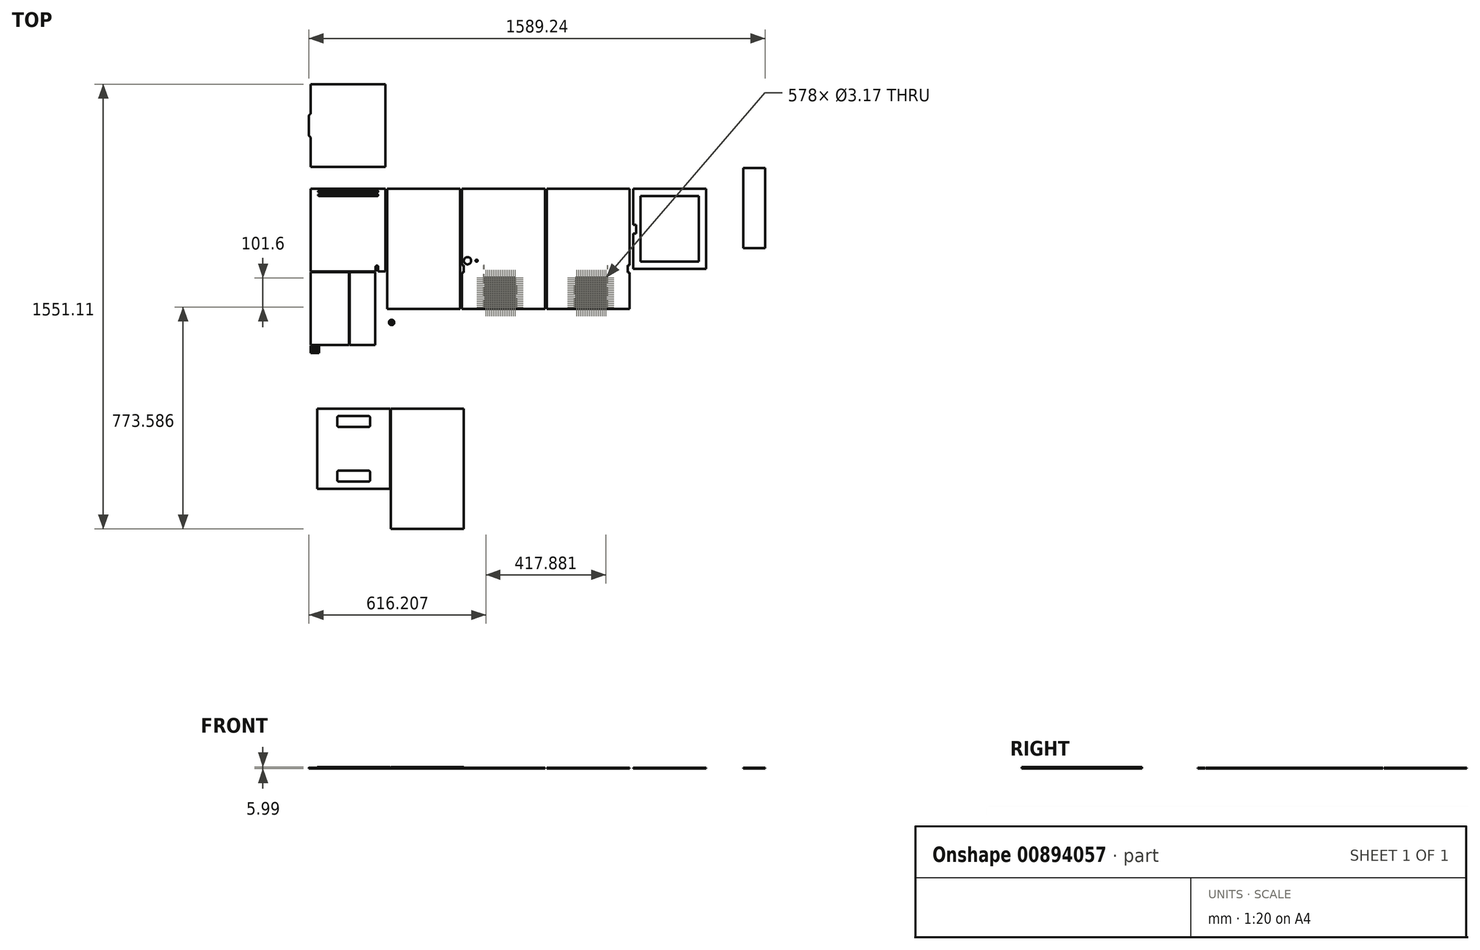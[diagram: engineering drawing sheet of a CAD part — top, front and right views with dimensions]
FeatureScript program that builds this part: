
annotation { "Feature Type Name" : "Feature", "Feature Type Description" : "" }
export const myFeature = defineFeature(function(context is Context, id is Id, definition is map)
    precondition{}
    {
        {
            var Q0;
            Q0=qCreatedBy(makeId("Top.planeOp"),FACE);
            var sketch = newSketch(context, id + "F0", { "sketchPlane" : qUnion([Q0])});
            skLineSegment(sketch, "E0.bottom", {"start": v(-364.9, 306.86) * mm, "end": v(-60.1, 306.86) * mm});
            skLineSegment(sketch, "E0.top", {"start": v(-364.9, -302.74) * mm, "end": v(-60.1, -302.74) * mm});
            skLineSegment(sketch, "E0.left", {"start": v(-364.9, 306.86) * mm, "end": v(-364.9, -302.74) * mm});
            skLineSegment(sketch, "E0.right", {"start": v(-60.1, 306.86) * mm, "end": v(-60.1, -302.74) * mm});
            skSolve(sketch);
        }
        {
            var Q0;
            Q0=makeQuery(id+"F0.imprint","IMPRINT",FACE,{"disambiguationData":[TD([[makeQuery(id+"F0.imprint","IMPRINT",EDGE,{"derivedFrom":sQuery(id+"F0.wireOp",EDGE,"E0.bottom")}),-1.0]])]});
            var sketch = newSketch(context, id + "F1", { "sketchPlane" : qUnion([Q0])});
            skPoint(sketch, "E1", {"position": v(-364.9, 306.86) * mm});
            skLineSegment(sketch, "E2.bottom", {"start": v(-364.9, 306.86) * mm, "end": v(-104.55, 306.86) * mm});
            skLineSegment(sketch, "E2.top", {"start": v(-364.9, 18.29) * mm, "end": v(-104.55, 18.29) * mm});
            skLineSegment(sketch, "E2.left", {"start": v(-364.9, 306.86) * mm, "end": v(-364.9, 18.29) * mm});
            skLineSegment(sketch, "E2.right", {"start": v(-104.55, 306.86) * mm, "end": v(-104.55, 18.29) * mm});
            skPoint(sketch, "E3", {"position": v(457.07, 306.86) * mm});
            skLineSegment(sketch, "E4.bottom", {"start": v(457.07, 306.86) * mm, "end": v(745.64, 306.86) * mm});
            skLineSegment(sketch, "E4.top", {"start": v(457.07, -112.24) * mm, "end": v(745.64, -112.24) * mm});
            skLineSegment(sketch, "E4.left", {"start": v(457.07, 306.86) * mm, "end": v(457.07, -112.24) * mm});
            skLineSegment(sketch, "E4.right", {"start": v(745.64, 306.86) * mm, "end": v(745.64, 40.16) * mm});
            skLineSegment(sketch, "E5.bottom", {"start": v(162.15, 306.86) * mm, "end": v(450.72, 306.86) * mm});
            skLineSegment(sketch, "E5.top", {"start": v(162.15, -112.24) * mm, "end": v(450.72, -112.24) * mm});
            skLineSegment(sketch, "E5.left", {"start": v(162.15, 306.86) * mm, "end": v(162.15, 40.16) * mm});
            skLineSegment(sketch, "E5.right", {"start": v(450.72, 306.86) * mm, "end": v(450.72, -112.24) * mm});
            skLineSegment(sketch, "E6.bottom", {"start": v(-98.2, 306.86) * mm, "end": v(155.8, 306.86) * mm});
            skLineSegment(sketch, "E6.top", {"start": v(-98.2, -112.24) * mm, "end": v(155.8, -112.24) * mm});
            skLineSegment(sketch, "E6.left", {"start": v(-98.2, 306.86) * mm, "end": v(-98.2, -112.24) * mm});
            skLineSegment(sketch, "E6.right", {"start": v(155.8, 306.86) * mm, "end": v(155.8, -112.24) * mm});
            skPoint(sketch, "E7", {"position": v(-229, 15.75) * mm});
            skLineSegment(sketch, "E8.bottom", {"start": v(-229, 15.75) * mm, "end": v(-140.1, 15.75) * mm});
            skLineSegment(sketch, "E8.top", {"start": v(-229, -238.25) * mm, "end": v(-140.1, -238.25) * mm});
            skLineSegment(sketch, "E8.left", {"start": v(-229, 15.75) * mm, "end": v(-229, -238.25) * mm});
            skLineSegment(sketch, "E8.right", {"start": v(-140.1, 15.75) * mm, "end": v(-140.1, -238.25) * mm});
            skLineSegment(sketch, "E9.bottom", {"start": v(162.15, 40.16) * mm, "end": v(168.5, 40.16) * mm});
            skLineSegment(sketch, "E9.top", {"start": v(162.15, 14.76) * mm, "end": v(168.5, 14.76) * mm});
            skLineSegment(sketch, "E9.right", {"start": v(168.5, 40.16) * mm, "end": v(168.5, 14.76) * mm});
            skLineSegment(sketch, "E10.trimOffspring", {"start": v(162.15, 14.76) * mm, "end": v(162.15, -112.24) * mm});
            skLineSegment(sketch, "E11", {"start": v(745.64, 40.16) * mm, "end": v(739.3, 40.16) * mm});
            skLineSegment(sketch, "E12", {"start": v(739.3, 40.16) * mm, "end": v(739.3, 14.76) * mm});
            skLineSegment(sketch, "E13", {"start": v(739.3, 14.76) * mm, "end": v(745.64, 14.76) * mm});
            skLineSegment(sketch, "E14.trimOffspring", {"start": v(745.64, 14.76) * mm, "end": v(745.64, -112.24) * mm});
            skLineSegment(sketch, "E15.bottom", {"start": v(-364.9, -238.25) * mm, "end": v(-231.55, -238.25) * mm});
            skLineSegment(sketch, "E15.top", {"start": v(-364.9, 15.75) * mm, "end": v(-231.55, 15.75) * mm});
            skLineSegment(sketch, "E15.left", {"start": v(-364.9, -238.25) * mm, "end": v(-364.9, 15.75) * mm});
            skLineSegment(sketch, "E15.right", {"start": v(-231.55, -238.25) * mm, "end": v(-231.55, 15.75) * mm});
            skCircle(sketch, "E16", {"center": v(-83.43, -156.52) * mm, "radius": 3.75 * mm});
            skCircle(sketch, "E17", {"center": v(-83.43, -164.32) * mm, "radius": 1.5 * mm});
            skCircle(sketch, "E18", {"center": v(-83.43, -159.38) * mm, "radius": 9.35 * mm});
            skLineSegment(sketch, "E19.bottom", {"start": v(-364.9, -240.8) * mm, "end": v(-358.55, -240.8) * mm});
            skLineSegment(sketch, "E19.top", {"start": v(-364.9, -266.2) * mm, "end": v(-358.55, -266.2) * mm});
            skLineSegment(sketch, "E19.left", {"start": v(-364.9, -240.8) * mm, "end": v(-364.9, -266.2) * mm});
            skLineSegment(sketch, "E19.right", {"start": v(-358.55, -240.8) * mm, "end": v(-358.55, -266.2) * mm});
            skLineSegment(sketch, "E20.bottom", {"start": v(-336.32, 300.5) * mm, "end": v(-133.12, 300.5) * mm});
            skLineSegment(sketch, "E20.top", {"start": v(-336.32, 294.16) * mm, "end": v(-133.12, 294.16) * mm});
            skLineSegment(sketch, "E21", {"start": v(-234.72, 306.86) * mm, "end": v(-234.72, 18.29) * mm, "construction": true});
            skPoint(sketch, "E22", {"position": v(-234.72, 300.5) * mm});
            skArc(sketch, "E23", {"start": v(-133.12, 294.16) * mm, "mid": v(-129.95, 297.33) * mm, "end": v(-133.12, 300.5) * mm});
            skArc(sketch, "E24", {"start": v(-336.32, 300.5) * mm, "mid": v(-339.5, 297.33) * mm, "end": v(-336.32, 294.16) * mm});
            skArc(sketch, "E25.0.1.0", {"start": v(-336.32, 287.8) * mm, "mid": v(-339.5, 284.63) * mm, "end": v(-336.32, 281.46) * mm});
            skLineSegment(sketch, "E25.0.1.1", {"start": v(-336.32, 287.8) * mm, "end": v(-133.12, 287.8) * mm});
            skArc(sketch, "E25.0.1.2", {"start": v(-133.12, 281.46) * mm, "mid": v(-129.95, 284.63) * mm, "end": v(-133.12, 287.8) * mm});
            skLineSegment(sketch, "E25.0.1.3", {"start": v(-336.32, 281.46) * mm, "end": v(-133.12, 281.46) * mm});
            skLineSegment(sketch, "E25.direction1", {"start": v(-336.32, 294.16) * mm, "end": v(-295.94, 294.16) * mm, "construction": true});
            skLineSegment(sketch, "E25.direction2", {"start": v(-336.32, 294.16) * mm, "end": v(-336.32, 281.46) * mm, "construction": true});
            skLineSegment(sketch, "E26.bottom", {"start": v(-129.95, 18.29) * mm, "end": v(-139.47, 18.29) * mm});
            skLineSegment(sketch, "E26.left", {"start": v(-129.95, 18.29) * mm, "end": v(-129.95, 34.16) * mm});
            skLineSegment(sketch, "E26.right", {"start": v(-139.47, 18.29) * mm, "end": v(-139.47, 34.16) * mm});
            skArc(sketch, "E27", {"start": v(-129.95, 34.16) * mm, "mid": v(-134.7, 38.92) * mm, "end": v(-139.47, 34.16) * mm});
            skLineSegment(sketch, "E28.1.0.0", {"start": v(-357.28, -240.8) * mm, "end": v(-357.28, -266.2) * mm});
            skLineSegment(sketch, "E28.1.0.1", {"start": v(-357.28, -240.8) * mm, "end": v(-350.93, -240.8) * mm});
            skLineSegment(sketch, "E28.1.0.2", {"start": v(-350.93, -240.8) * mm, "end": v(-350.93, -266.2) * mm});
            skLineSegment(sketch, "E28.1.0.3", {"start": v(-357.28, -266.2) * mm, "end": v(-350.93, -266.2) * mm});
            skLineSegment(sketch, "E28.2.0.0", {"start": v(-349.66, -240.8) * mm, "end": v(-349.66, -266.2) * mm});
            skLineSegment(sketch, "E28.2.0.1", {"start": v(-349.66, -240.8) * mm, "end": v(-343.3, -240.8) * mm});
            skLineSegment(sketch, "E28.2.0.2", {"start": v(-343.3, -240.8) * mm, "end": v(-343.3, -266.2) * mm});
            skLineSegment(sketch, "E28.2.0.3", {"start": v(-349.66, -266.2) * mm, "end": v(-343.3, -266.2) * mm});
            skLineSegment(sketch, "E28.3.0.0", {"start": v(-342.04, -240.8) * mm, "end": v(-342.04, -266.2) * mm});
            skLineSegment(sketch, "E28.3.0.1", {"start": v(-342.04, -240.8) * mm, "end": v(-335.69, -240.8) * mm});
            skLineSegment(sketch, "E28.3.0.2", {"start": v(-335.69, -240.8) * mm, "end": v(-335.69, -266.2) * mm});
            skLineSegment(sketch, "E28.3.0.3", {"start": v(-342.04, -266.2) * mm, "end": v(-335.69, -266.2) * mm});
            skLineSegment(sketch, "E28.direction1", {"start": v(-364.9, -266.2) * mm, "end": v(-357.28, -266.2) * mm, "construction": true});
            skLineSegment(sketch, "E29.bottom", {"start": v(758.34, 306.86) * mm, "end": v(1012.34, 306.86) * mm});
            skLineSegment(sketch, "E29.top", {"start": v(758.34, 27.46) * mm, "end": v(1012.34, 27.46) * mm});
            skLineSegment(sketch, "E29.left", {"start": v(758.34, 306.86) * mm, "end": v(758.34, 27.46) * mm});
            skLineSegment(sketch, "E29.right", {"start": v(1012.34, 306.86) * mm, "end": v(1012.34, 27.46) * mm});
            skLineSegment(sketch, "E30.0", {"start": v(783.74, 281.46) * mm, "end": v(986.94, 281.46) * mm});
            skLineSegment(sketch, "E30.1", {"start": v(783.74, 281.46) * mm, "end": v(783.74, 52.86) * mm});
            skLineSegment(sketch, "E30.2", {"start": v(783.74, 52.86) * mm, "end": v(986.94, 52.86) * mm});
            skLineSegment(sketch, "E30.3", {"start": v(986.94, 281.46) * mm, "end": v(986.94, 52.86) * mm});
            skLineSegment(sketch, "E31.bottom", {"start": v(758.34, 181.62) * mm, "end": v(768.58, 181.62) * mm});
            skLineSegment(sketch, "E31.top", {"start": v(758.34, 151.14) * mm, "end": v(768.58, 151.14) * mm});
            skLineSegment(sketch, "E31.left", {"start": v(758.34, 181.62) * mm, "end": v(758.34, 151.14) * mm});
            skLineSegment(sketch, "E31.right", {"start": v(768.58, 181.62) * mm, "end": v(768.58, 151.14) * mm});
            skLineSegment(sketch, "E32.bottom", {"start": v(1141.79, 379.02) * mm, "end": v(1217.99, 379.02) * mm});
            skLineSegment(sketch, "E32.top", {"start": v(1141.79, 99.62) * mm, "end": v(1217.99, 99.62) * mm});
            skLineSegment(sketch, "E32.left", {"start": v(1141.79, 379.02) * mm, "end": v(1141.79, 99.62) * mm});
            skLineSegment(sketch, "E32.right", {"start": v(1217.99, 379.02) * mm, "end": v(1217.99, 99.62) * mm});
            skSolve(sketch);
        }
        {
            var Q0;
            Q0=makeQuery(id+"F1.imprint","IMPRINT",FACE,{"disambiguationData":[TD([[makeQuery(id+"F1.imprint","IMPRINT",EDGE,{"derivedFrom":sQuery(id+"F1.wireOp",EDGE,"E2.bottom")}),-1.0]])]});
            var Q1;
            Q1=makeQuery(id+"F1.imprint","IMPRINT",FACE,{"disambiguationData":[TD([[makeQuery(id+"F1.imprint","IMPRINT",EDGE,{"derivedFrom":sQuery(id+"F1.wireOp",EDGE,"E6.bottom")}),-1.0]])]});
            var Q2;
            Q2=makeQuery(id+"F1.imprint","IMPRINT",FACE,{"disambiguationData":[TD([[makeQuery(id+"F1.imprint","IMPRINT",EDGE,{"derivedFrom":sQuery(id+"F1.wireOp",EDGE,"E4.bottom")}),-1.0]])]});
            var Q3;
            Q3=makeQuery(id+"F1.imprint","IMPRINT",FACE,{"disambiguationData":[TD([[makeQuery(id+"F1.imprint","IMPRINT",EDGE,{"derivedFrom":sQuery(id+"F1.wireOp",EDGE,"E5.bottom")}),-1.0]])]});
            var Q4;
            Q4=makeQuery(id+"F1.imprint","IMPRINT",FACE,{"disambiguationData":[TD([[makeQuery(id+"F1.imprint","IMPRINT",EDGE,{"derivedFrom":sQuery(id+"F1.wireOp",EDGE,"E8.bottom")}),-1.0]])]});
            var Q5;
            Q5=makeQuery(id+"F1.imprint","IMPRINT",FACE,{"disambiguationData":[TD([[makeQuery(id+"F1.imprint","IMPRINT",EDGE,{"derivedFrom":sQuery(id+"F1.wireOp",EDGE,"E15.bottom")}),1.0]])]});
            var Q6;
            Q6=makeQuery(id+"F1.imprint","IMPRINT",FACE,{"disambiguationData":[TD([[makeQuery(id+"F1.imprint","IMPRINT",EDGE,{"derivedFrom":sQuery(id+"F1.wireOp",EDGE,"E16")}),-1.0]])]});
            var Q7;
            Q7=makeQuery(id+"F1.imprint","IMPRINT",FACE,{"disambiguationData":[TD([[makeQuery(id+"F1.imprint","IMPRINT",EDGE,{"derivedFrom":sQuery(id+"F1.wireOp",EDGE,"E19.bottom")}),-1.0]])]});
            var Q8;
            Q8=makeQuery(id+"F1.imprint","IMPRINT",FACE,{"disambiguationData":[TD([[makeQuery(id+"F1.imprint","IMPRINT",EDGE,{"derivedFrom":sQuery(id+"F1.wireOp",EDGE,"IQMkBjuR-eJGy-Trob-1RJN-rlCJfxQlDLsO.bottom")}),-1.0]])]});
            var Q9;
            Q9=makeQuery(id+"F1.imprint","IMPRINT",FACE,{"disambiguationData":[TD([[makeQuery(id+"F1.imprint","IMPRINT",EDGE,{"derivedFrom":sQuery(id+"F1.wireOp",EDGE,"E28.1.0.0")}),1.0]])]});
            var Q10;
            Q10=makeQuery(id+"F1.imprint","IMPRINT",FACE,{"disambiguationData":[TD([[makeQuery(id+"F1.imprint","IMPRINT",EDGE,{"derivedFrom":sQuery(id+"F1.wireOp",EDGE,"E28.2.0.0")}),1.0]])]});
            var Q11;
            Q11=makeQuery(id+"F1.imprint","IMPRINT",FACE,{"disambiguationData":[TD([[makeQuery(id+"F1.imprint","IMPRINT",EDGE,{"derivedFrom":sQuery(id+"F1.wireOp",EDGE,"E28.3.0.0")}),1.0]])]});
            var Q12;
            Q12=makeQuery(id+"F1.imprint","IMPRINT",FACE,{"disambiguationData":[TD([[makeQuery(id+"F1.imprint","IMPRINT",EDGE,{"derivedFrom":sQuery(id+"F1.wireOp",EDGE,"E29.bottom")}),-1.0]])]});
            var Q13;
            Q13=makeQuery(id+"F1.imprint","IMPRINT",FACE,{"disambiguationData":[TD([[makeQuery(id+"F1.imprint","IMPRINT",EDGE,{"derivedFrom":sQuery(id+"F1.wireOp",EDGE,"E32.bottom")}),-1.0]])]});
            extrude(context, id + "F2", {"entities" : qUnion([Q0, Q1, Q2, Q3, Q4, Q5, Q6, Q7, Q8, Q9, Q10, Q11, Q12, Q13]), "depth" : 3.17 * mm, "offsetDistance" : 25.4 * mm});
        }
        {
            var Q0;
            Q0=qCreatedBy(makeId("Top.planeOp"),FACE);
            var sketch = newSketch(context, id + "F3", { "sketchPlane" : qUnion([Q0])});
            skLineSegment(sketch, "E33.bottom", {"start": v(-342.67, -460.38) * mm, "end": v(266.93, -460.38) * mm});
            skLineSegment(sketch, "E33.top", {"start": v(-342.67, -1069.98) * mm, "end": v(266.93, -1069.98) * mm});
            skLineSegment(sketch, "E33.left", {"start": v(-342.67, -460.38) * mm, "end": v(-342.67, -1069.98) * mm});
            skLineSegment(sketch, "E33.right", {"start": v(266.93, -460.38) * mm, "end": v(266.93, -1069.98) * mm});
            skSolve(sketch);
        }
        {
            var Q0;
            Q0=makeQuery(id+"F3.imprint","IMPRINT",FACE,{"disambiguationData":[TD([[makeQuery(id+"F3.imprint","IMPRINT",EDGE,{"derivedFrom":sQuery(id+"F3.wireOp",EDGE,"E33.bottom")}),-1.0]])]});
            var sketch = newSketch(context, id + "F4", { "sketchPlane" : qUnion([Q0])});
            skPoint(sketch, "E34", {"position": v(-342.67, -460.38) * mm});
            skLineSegment(sketch, "E35.bottom", {"start": v(-342.67, -460.38) * mm, "end": v(-88.67, -460.38) * mm});
            skLineSegment(sketch, "E35.top", {"start": v(-342.67, -739.78) * mm, "end": v(-88.67, -739.78) * mm});
            skLineSegment(sketch, "E35.left", {"start": v(-342.67, -460.38) * mm, "end": v(-342.67, -739.78) * mm});
            skLineSegment(sketch, "E35.right", {"start": v(-88.67, -460.38) * mm, "end": v(-88.67, -739.78) * mm});
            skLineSegment(sketch, "E36", {"start": v(-215.67, -460.38) * mm, "end": v(-215.67, -739.78) * mm, "construction": true});
            skLineSegment(sketch, "E37.bottom", {"start": v(-158.52, -485.78) * mm, "end": v(-272.82, -485.78) * mm});
            skLineSegment(sketch, "E37.top", {"start": v(-158.52, -523.88) * mm, "end": v(-272.82, -523.88) * mm});
            skLineSegment(sketch, "E37.left", {"start": v(-158.52, -485.78) * mm, "end": v(-158.52, -523.88) * mm});
            skLineSegment(sketch, "E37.right", {"start": v(-272.82, -485.78) * mm, "end": v(-272.82, -523.88) * mm});
            skPoint(sketch, "E37.middle", {"position": v(-215.67, -504.83) * mm});
            skLineSegment(sketch, "E38.bottom", {"start": v(-158.52, -676.28) * mm, "end": v(-272.82, -676.28) * mm});
            skLineSegment(sketch, "E38.top", {"start": v(-158.52, -714.38) * mm, "end": v(-272.82, -714.38) * mm});
            skLineSegment(sketch, "E38.left", {"start": v(-158.52, -676.28) * mm, "end": v(-158.52, -714.38) * mm});
            skLineSegment(sketch, "E38.right", {"start": v(-272.82, -676.28) * mm, "end": v(-272.82, -714.38) * mm});
            skPoint(sketch, "E38.middle", {"position": v(-215.67, -695.33) * mm});
            skPoint(sketch, "E39", {"position": v(-85.5, -460.38) * mm});
            skLineSegment(sketch, "E40.bottom", {"start": v(-85.5, -460.38) * mm, "end": v(168.5, -460.38) * mm});
            skLineSegment(sketch, "E40.top", {"start": v(-85.5, -879.48) * mm, "end": v(168.5, -879.48) * mm});
            skLineSegment(sketch, "E40.left", {"start": v(-85.5, -460.38) * mm, "end": v(-85.5, -879.48) * mm});
            skLineSegment(sketch, "E40.right", {"start": v(168.5, -460.38) * mm, "end": v(168.5, -879.48) * mm});
            skSolve(sketch);
        }
        {
            var Q0;
            Q0 = qSketchRegion(id + "F4", true);
            extrude(context, id + "F5", {"entities" : qUnion([Q0]), "depth" : 6 * mm, "offsetDistance" : 25.4 * mm});
        }
        {
            var Q0;
            Q0=makeQuery(id+"F2.opExtrude","CAP_FACE",FACE,{"disambiguationData":[OSD([sQuery(id+"F1.wireOp",EDGE,"E5.bottom"),sQuery(id+"F1.wireOp",EDGE,"E5.top"),sQuery(id+"F1.wireOp",EDGE,"E5.left"),sQuery(id+"F1.wireOp",EDGE,"E5.right"),sQuery(id+"F1.wireOp",EDGE,"E9.bottom"),sQuery(id+"F1.wireOp",EDGE,"E9.top"),sQuery(id+"F1.wireOp",EDGE,"E9.right"),sQuery(id+"F1.wireOp",EDGE,"E10.trimOffspring")])],"isStart":true});
            var sketch = newSketch(context, id + "F6", { "sketchPlane" : qUnion([Q0])});
            skLineSegment(sketch, "E41.bottom", {"start": v(353.03, 104.4) * mm, "end": v(353.29, 104.4) * mm});
            skLineSegment(sketch, "E41.top", {"start": v(353.03, 15.5) * mm, "end": v(353.29, 15.5) * mm});
            skLineSegment(sketch, "E41.left", {"start": v(353.03, 104.4) * mm, "end": v(353.03, 15.5) * mm});
            skLineSegment(sketch, "E41.right", {"start": v(353.29, 104.4) * mm, "end": v(353.29, 15.5) * mm});
            skLineSegment(sketch, "E42.bottom", {"start": v(238.6, 112.24) * mm, "end": v(238.35, 112.24) * mm});
            skLineSegment(sketch, "E42.top", {"start": v(238.6, -40.16) * mm, "end": v(238.35, -40.16) * mm});
            skLineSegment(sketch, "E42.left", {"start": v(238.6, 112.24) * mm, "end": v(238.6, -40.16) * mm});
            skLineSegment(sketch, "E42.right", {"start": v(238.35, 112.24) * mm, "end": v(238.35, -40.16) * mm});
            skSolve(sketch);
        }
        {
            var Q0;
            Q0 = qSketchRegion(id + "F6", true);
            extrude(context, id + "F7", {"entities" : qUnion([Q0]), "operationType" : NewBodyOperationType.REMOVE, "oppositeDirection" : true, "depth" : 0.5 * mm, "offsetDistance" : 25.4 * mm});
        }
        {
            var Q0;
            Q0=makeQuery(id+"F2.opExtrude","CAP_FACE",FACE,{"disambiguationData":[OSD([sQuery(id+"F1.wireOp",EDGE,"E4.bottom"),sQuery(id+"F1.wireOp",EDGE,"E4.top"),sQuery(id+"F1.wireOp",EDGE,"E4.left"),sQuery(id+"F1.wireOp",EDGE,"E4.right"),sQuery(id+"F1.wireOp",EDGE,"E11"),sQuery(id+"F1.wireOp",EDGE,"E12"),sQuery(id+"F1.wireOp",EDGE,"E13"),sQuery(id+"F1.wireOp",EDGE,"E14.trimOffspring")])],"isStart":true});
            var sketch = newSketch(context, id + "F8", { "sketchPlane" : qUnion([Q0])});
            skLineSegment(sketch, "E43.bottom", {"start": v(554.5, 104.4) * mm, "end": v(554.76, 104.4) * mm});
            skLineSegment(sketch, "E43.top", {"start": v(554.5, 15.5) * mm, "end": v(554.76, 15.5) * mm});
            skLineSegment(sketch, "E43.left", {"start": v(554.5, 104.4) * mm, "end": v(554.5, 15.5) * mm});
            skLineSegment(sketch, "E43.right", {"start": v(554.76, 104.4) * mm, "end": v(554.76, 15.5) * mm});
            skLineSegment(sketch, "E44.bottom", {"start": v(669.19, 112.24) * mm, "end": v(669.44, 112.24) * mm});
            skLineSegment(sketch, "E44.top", {"start": v(669.19, -40.16) * mm, "end": v(669.44, -40.16) * mm});
            skLineSegment(sketch, "E44.left", {"start": v(669.19, 112.24) * mm, "end": v(669.19, -40.16) * mm});
            skLineSegment(sketch, "E44.right", {"start": v(669.44, 112.24) * mm, "end": v(669.44, -40.16) * mm});
            skSolve(sketch);
        }
        {
            var Q0;
            Q0 = qSketchRegion(id + "F8", true);
            extrude(context, id + "F9", {"entities" : qUnion([Q0]), "operationType" : NewBodyOperationType.REMOVE, "oppositeDirection" : true, "depth" : 0.5 * mm, "offsetDistance" : 25.4 * mm});
        }
        {
            var Q0;
            Q0=makeQuery(id+"F2.opExtrude","CAP_FACE",FACE,{"disambiguationData":[OSD([sQuery(id+"F1.wireOp",EDGE,"E5.bottom"),sQuery(id+"F1.wireOp",EDGE,"E5.top"),sQuery(id+"F1.wireOp",EDGE,"E5.left"),sQuery(id+"F1.wireOp",EDGE,"E5.right"),sQuery(id+"F1.wireOp",EDGE,"E9.bottom"),sQuery(id+"F1.wireOp",EDGE,"E9.top"),sQuery(id+"F1.wireOp",EDGE,"E9.right"),sQuery(id+"F1.wireOp",EDGE,"E10.trimOffspring")])],"isStart":true});
            var sketch = newSketch(context, id + "F10", { "sketchPlane" : qUnion([Q0])});
            skLineSegment(sketch, "E45.bottom", {"start": v(244.96, 105.9) * mm, "end": v(346.68, 105.9) * mm, "construction": true});
            skLineSegment(sketch, "E45.top", {"start": v(244.96, 4.3) * mm, "end": v(346.68, 4.3) * mm, "construction": true});
            skLineSegment(sketch, "E45.left", {"start": v(244.96, 105.9) * mm, "end": v(244.96, 4.3) * mm, "construction": true});
            skLineSegment(sketch, "E45.right", {"start": v(346.68, 105.9) * mm, "end": v(346.68, 4.3) * mm, "construction": true});
            skCircle(sketch, "E46", {"center": v(244.96, 4.3) * mm, "radius": 1.59 * mm});
            skCircle(sketch, "E47.0.1.0", {"center": v(244.96, 10.64) * mm, "radius": 1.59 * mm});
            skCircle(sketch, "E47.0.2.0", {"center": v(244.96, 17) * mm, "radius": 1.59 * mm});
            skCircle(sketch, "E47.0.3.0", {"center": v(244.96, 23.34) * mm, "radius": 1.59 * mm});
            skCircle(sketch, "E47.0.4.0", {"center": v(244.96, 29.7) * mm, "radius": 1.59 * mm});
            skCircle(sketch, "E47.0.5.0", {"center": v(244.96, 36.04) * mm, "radius": 1.59 * mm});
            skCircle(sketch, "E47.0.6.0", {"center": v(244.96, 42.4) * mm, "radius": 1.59 * mm});
            skCircle(sketch, "E47.0.7.0", {"center": v(244.96, 48.74) * mm, "radius": 1.59 * mm});
            skCircle(sketch, "E47.0.8.0", {"center": v(244.96, 55.1) * mm, "radius": 1.59 * mm});
            skCircle(sketch, "E47.0.9.0", {"center": v(244.96, 61.44) * mm, "radius": 1.59 * mm});
            skCircle(sketch, "E47.0.10.0", {"center": v(244.96, 67.8) * mm, "radius": 1.59 * mm});
            skCircle(sketch, "E47.0.11.0", {"center": v(244.96, 74.14) * mm, "radius": 1.59 * mm});
            skCircle(sketch, "E47.0.12.0", {"center": v(244.96, 80.5) * mm, "radius": 1.59 * mm});
            skCircle(sketch, "E47.0.13.0", {"center": v(244.96, 86.84) * mm, "radius": 1.59 * mm});
            skCircle(sketch, "E47.0.14.0", {"center": v(244.96, 93.2) * mm, "radius": 1.59 * mm});
            skCircle(sketch, "E47.0.15.0", {"center": v(244.96, 99.54) * mm, "radius": 1.59 * mm});
            skCircle(sketch, "E47.0.16.0", {"center": v(244.96, 105.9) * mm, "radius": 1.59 * mm});
            skCircle(sketch, "E47.1.0.0", {"center": v(251.3, 4.3) * mm, "radius": 1.59 * mm});
            skCircle(sketch, "E47.1.1.0", {"center": v(251.3, 10.64) * mm, "radius": 1.59 * mm});
            skCircle(sketch, "E47.1.2.0", {"center": v(251.3, 17) * mm, "radius": 1.59 * mm});
            skCircle(sketch, "E47.1.3.0", {"center": v(251.3, 23.34) * mm, "radius": 1.59 * mm});
            skCircle(sketch, "E47.1.4.0", {"center": v(251.3, 29.7) * mm, "radius": 1.59 * mm});
            skCircle(sketch, "E47.1.5.0", {"center": v(251.3, 36.04) * mm, "radius": 1.59 * mm});
            skCircle(sketch, "E47.1.6.0", {"center": v(251.3, 42.4) * mm, "radius": 1.59 * mm});
            skCircle(sketch, "E47.1.7.0", {"center": v(251.3, 48.74) * mm, "radius": 1.59 * mm});
            skCircle(sketch, "E47.1.8.0", {"center": v(251.3, 55.1) * mm, "radius": 1.59 * mm});
            skCircle(sketch, "E47.1.9.0", {"center": v(251.3, 61.44) * mm, "radius": 1.59 * mm});
            skCircle(sketch, "E47.1.10.0", {"center": v(251.3, 67.8) * mm, "radius": 1.59 * mm});
            skCircle(sketch, "E47.1.11.0", {"center": v(251.3, 74.14) * mm, "radius": 1.59 * mm});
            skCircle(sketch, "E47.1.12.0", {"center": v(251.3, 80.5) * mm, "radius": 1.59 * mm});
            skCircle(sketch, "E47.1.13.0", {"center": v(251.3, 86.84) * mm, "radius": 1.59 * mm});
            skCircle(sketch, "E47.1.14.0", {"center": v(251.3, 93.2) * mm, "radius": 1.59 * mm});
            skCircle(sketch, "E47.1.15.0", {"center": v(251.3, 99.54) * mm, "radius": 1.59 * mm});
            skCircle(sketch, "E47.1.16.0", {"center": v(251.3, 105.9) * mm, "radius": 1.59 * mm});
            skCircle(sketch, "E47.2.0.0", {"center": v(257.66, 4.3) * mm, "radius": 1.59 * mm});
            skCircle(sketch, "E47.2.1.0", {"center": v(257.66, 10.64) * mm, "radius": 1.59 * mm});
            skCircle(sketch, "E47.2.2.0", {"center": v(257.66, 17) * mm, "radius": 1.59 * mm});
            skCircle(sketch, "E47.2.3.0", {"center": v(257.66, 23.34) * mm, "radius": 1.59 * mm});
            skCircle(sketch, "E47.2.4.0", {"center": v(257.66, 29.7) * mm, "radius": 1.59 * mm});
            skCircle(sketch, "E47.2.5.0", {"center": v(257.66, 36.04) * mm, "radius": 1.59 * mm});
            skCircle(sketch, "E47.2.6.0", {"center": v(257.66, 42.4) * mm, "radius": 1.59 * mm});
            skCircle(sketch, "E47.2.7.0", {"center": v(257.66, 48.74) * mm, "radius": 1.59 * mm});
            skCircle(sketch, "E47.2.8.0", {"center": v(257.66, 55.1) * mm, "radius": 1.59 * mm});
            skCircle(sketch, "E47.2.9.0", {"center": v(257.66, 61.44) * mm, "radius": 1.59 * mm});
            skCircle(sketch, "E47.2.10.0", {"center": v(257.66, 67.8) * mm, "radius": 1.59 * mm});
            skCircle(sketch, "E47.2.11.0", {"center": v(257.66, 74.14) * mm, "radius": 1.59 * mm});
            skCircle(sketch, "E47.2.12.0", {"center": v(257.66, 80.5) * mm, "radius": 1.59 * mm});
            skCircle(sketch, "E47.2.13.0", {"center": v(257.66, 86.84) * mm, "radius": 1.59 * mm});
            skCircle(sketch, "E47.2.14.0", {"center": v(257.66, 93.2) * mm, "radius": 1.59 * mm});
            skCircle(sketch, "E47.2.15.0", {"center": v(257.66, 99.54) * mm, "radius": 1.59 * mm});
            skCircle(sketch, "E47.2.16.0", {"center": v(257.66, 105.9) * mm, "radius": 1.59 * mm});
            skCircle(sketch, "E47.3.0.0", {"center": v(264, 4.3) * mm, "radius": 1.59 * mm});
            skCircle(sketch, "E47.3.1.0", {"center": v(264, 10.64) * mm, "radius": 1.59 * mm});
            skCircle(sketch, "E47.3.2.0", {"center": v(264, 17) * mm, "radius": 1.59 * mm});
            skCircle(sketch, "E47.3.3.0", {"center": v(264, 23.34) * mm, "radius": 1.59 * mm});
            skCircle(sketch, "E47.3.4.0", {"center": v(264, 29.7) * mm, "radius": 1.59 * mm});
            skCircle(sketch, "E47.3.5.0", {"center": v(264, 36.04) * mm, "radius": 1.59 * mm});
            skCircle(sketch, "E47.3.6.0", {"center": v(264, 42.4) * mm, "radius": 1.59 * mm});
            skCircle(sketch, "E47.3.7.0", {"center": v(264, 48.74) * mm, "radius": 1.59 * mm});
            skCircle(sketch, "E47.3.8.0", {"center": v(264, 55.1) * mm, "radius": 1.59 * mm});
            skCircle(sketch, "E47.3.9.0", {"center": v(264, 61.44) * mm, "radius": 1.59 * mm});
            skCircle(sketch, "E47.3.10.0", {"center": v(264, 67.8) * mm, "radius": 1.59 * mm});
            skCircle(sketch, "E47.3.11.0", {"center": v(264, 74.14) * mm, "radius": 1.59 * mm});
            skCircle(sketch, "E47.3.12.0", {"center": v(264, 80.5) * mm, "radius": 1.59 * mm});
            skCircle(sketch, "E47.3.13.0", {"center": v(264, 86.84) * mm, "radius": 1.59 * mm});
            skCircle(sketch, "E47.3.14.0", {"center": v(264, 93.2) * mm, "radius": 1.59 * mm});
            skCircle(sketch, "E47.3.15.0", {"center": v(264, 99.54) * mm, "radius": 1.59 * mm});
            skCircle(sketch, "E47.3.16.0", {"center": v(264, 105.9) * mm, "radius": 1.59 * mm});
            skCircle(sketch, "E47.4.0.0", {"center": v(270.36, 4.3) * mm, "radius": 1.59 * mm});
            skCircle(sketch, "E47.4.1.0", {"center": v(270.36, 10.64) * mm, "radius": 1.59 * mm});
            skCircle(sketch, "E47.4.2.0", {"center": v(270.36, 17) * mm, "radius": 1.59 * mm});
            skCircle(sketch, "E47.4.3.0", {"center": v(270.36, 23.34) * mm, "radius": 1.59 * mm});
            skCircle(sketch, "E47.4.4.0", {"center": v(270.36, 29.7) * mm, "radius": 1.59 * mm});
            skCircle(sketch, "E47.4.5.0", {"center": v(270.36, 36.04) * mm, "radius": 1.59 * mm});
            skCircle(sketch, "E47.4.6.0", {"center": v(270.36, 42.4) * mm, "radius": 1.59 * mm});
            skCircle(sketch, "E47.4.7.0", {"center": v(270.36, 48.74) * mm, "radius": 1.59 * mm});
            skCircle(sketch, "E47.4.8.0", {"center": v(270.36, 55.1) * mm, "radius": 1.59 * mm});
            skCircle(sketch, "E47.4.9.0", {"center": v(270.36, 61.44) * mm, "radius": 1.59 * mm});
            skCircle(sketch, "E47.4.10.0", {"center": v(270.36, 67.8) * mm, "radius": 1.59 * mm});
            skCircle(sketch, "E47.4.11.0", {"center": v(270.36, 74.14) * mm, "radius": 1.59 * mm});
            skCircle(sketch, "E47.4.12.0", {"center": v(270.36, 80.5) * mm, "radius": 1.59 * mm});
            skCircle(sketch, "E47.4.13.0", {"center": v(270.36, 86.84) * mm, "radius": 1.59 * mm});
            skCircle(sketch, "E47.4.14.0", {"center": v(270.36, 93.2) * mm, "radius": 1.59 * mm});
            skCircle(sketch, "E47.4.15.0", {"center": v(270.36, 99.54) * mm, "radius": 1.59 * mm});
            skCircle(sketch, "E47.4.16.0", {"center": v(270.36, 105.9) * mm, "radius": 1.59 * mm});
            skCircle(sketch, "E47.5.0.0", {"center": v(276.7, 4.3) * mm, "radius": 1.59 * mm});
            skCircle(sketch, "E47.5.1.0", {"center": v(276.7, 10.64) * mm, "radius": 1.59 * mm});
            skCircle(sketch, "E47.5.2.0", {"center": v(276.7, 17) * mm, "radius": 1.59 * mm});
            skCircle(sketch, "E47.5.3.0", {"center": v(276.7, 23.34) * mm, "radius": 1.59 * mm});
            skCircle(sketch, "E47.5.4.0", {"center": v(276.7, 29.7) * mm, "radius": 1.59 * mm});
            skCircle(sketch, "E47.5.5.0", {"center": v(276.7, 36.04) * mm, "radius": 1.59 * mm});
            skCircle(sketch, "E47.5.6.0", {"center": v(276.7, 42.4) * mm, "radius": 1.59 * mm});
            skCircle(sketch, "E47.5.7.0", {"center": v(276.7, 48.74) * mm, "radius": 1.59 * mm});
            skCircle(sketch, "E47.5.8.0", {"center": v(276.7, 55.1) * mm, "radius": 1.59 * mm});
            skCircle(sketch, "E47.5.9.0", {"center": v(276.7, 61.44) * mm, "radius": 1.59 * mm});
            skCircle(sketch, "E47.5.10.0", {"center": v(276.7, 67.8) * mm, "radius": 1.59 * mm});
            skCircle(sketch, "E47.5.11.0", {"center": v(276.7, 74.14) * mm, "radius": 1.59 * mm});
            skCircle(sketch, "E47.5.12.0", {"center": v(276.7, 80.5) * mm, "radius": 1.59 * mm});
            skCircle(sketch, "E47.5.13.0", {"center": v(276.7, 86.84) * mm, "radius": 1.59 * mm});
            skCircle(sketch, "E47.5.14.0", {"center": v(276.7, 93.2) * mm, "radius": 1.59 * mm});
            skCircle(sketch, "E47.5.15.0", {"center": v(276.7, 99.54) * mm, "radius": 1.59 * mm});
            skCircle(sketch, "E47.5.16.0", {"center": v(276.7, 105.9) * mm, "radius": 1.59 * mm});
            skCircle(sketch, "E47.6.0.0", {"center": v(283.06, 4.3) * mm, "radius": 1.59 * mm});
            skCircle(sketch, "E47.6.1.0", {"center": v(283.06, 10.64) * mm, "radius": 1.59 * mm});
            skCircle(sketch, "E47.6.2.0", {"center": v(283.06, 17) * mm, "radius": 1.59 * mm});
            skCircle(sketch, "E47.6.3.0", {"center": v(283.06, 23.34) * mm, "radius": 1.59 * mm});
            skCircle(sketch, "E47.6.4.0", {"center": v(283.06, 29.7) * mm, "radius": 1.59 * mm});
            skCircle(sketch, "E47.6.5.0", {"center": v(283.06, 36.04) * mm, "radius": 1.59 * mm});
            skCircle(sketch, "E47.6.6.0", {"center": v(283.06, 42.4) * mm, "radius": 1.59 * mm});
            skCircle(sketch, "E47.6.7.0", {"center": v(283.06, 48.74) * mm, "radius": 1.59 * mm});
            skCircle(sketch, "E47.6.8.0", {"center": v(283.06, 55.1) * mm, "radius": 1.59 * mm});
            skCircle(sketch, "E47.6.9.0", {"center": v(283.06, 61.44) * mm, "radius": 1.59 * mm});
            skCircle(sketch, "E47.6.10.0", {"center": v(283.06, 67.8) * mm, "radius": 1.59 * mm});
            skCircle(sketch, "E47.6.11.0", {"center": v(283.06, 74.14) * mm, "radius": 1.59 * mm});
            skCircle(sketch, "E47.6.12.0", {"center": v(283.06, 80.5) * mm, "radius": 1.59 * mm});
            skCircle(sketch, "E47.6.13.0", {"center": v(283.06, 86.84) * mm, "radius": 1.59 * mm});
            skCircle(sketch, "E47.6.14.0", {"center": v(283.06, 93.2) * mm, "radius": 1.59 * mm});
            skCircle(sketch, "E47.6.15.0", {"center": v(283.06, 99.54) * mm, "radius": 1.59 * mm});
            skCircle(sketch, "E47.6.16.0", {"center": v(283.06, 105.9) * mm, "radius": 1.59 * mm});
            skCircle(sketch, "E47.7.0.0", {"center": v(289.4, 4.3) * mm, "radius": 1.59 * mm});
            skCircle(sketch, "E47.7.1.0", {"center": v(289.4, 10.64) * mm, "radius": 1.59 * mm});
            skCircle(sketch, "E47.7.2.0", {"center": v(289.4, 17) * mm, "radius": 1.59 * mm});
            skCircle(sketch, "E47.7.3.0", {"center": v(289.4, 23.34) * mm, "radius": 1.59 * mm});
            skCircle(sketch, "E47.7.4.0", {"center": v(289.4, 29.7) * mm, "radius": 1.59 * mm});
            skCircle(sketch, "E47.7.5.0", {"center": v(289.4, 36.04) * mm, "radius": 1.59 * mm});
            skCircle(sketch, "E47.7.6.0", {"center": v(289.4, 42.4) * mm, "radius": 1.59 * mm});
            skCircle(sketch, "E47.7.7.0", {"center": v(289.4, 48.74) * mm, "radius": 1.59 * mm});
            skCircle(sketch, "E47.7.8.0", {"center": v(289.4, 55.1) * mm, "radius": 1.59 * mm});
            skCircle(sketch, "E47.7.9.0", {"center": v(289.4, 61.44) * mm, "radius": 1.59 * mm});
            skCircle(sketch, "E47.7.10.0", {"center": v(289.4, 67.8) * mm, "radius": 1.59 * mm});
            skCircle(sketch, "E47.7.11.0", {"center": v(289.4, 74.14) * mm, "radius": 1.59 * mm});
            skCircle(sketch, "E47.7.12.0", {"center": v(289.4, 80.5) * mm, "radius": 1.59 * mm});
            skCircle(sketch, "E47.7.13.0", {"center": v(289.4, 86.84) * mm, "radius": 1.59 * mm});
            skCircle(sketch, "E47.7.14.0", {"center": v(289.4, 93.2) * mm, "radius": 1.59 * mm});
            skCircle(sketch, "E47.7.15.0", {"center": v(289.4, 99.54) * mm, "radius": 1.59 * mm});
            skCircle(sketch, "E47.7.16.0", {"center": v(289.4, 105.9) * mm, "radius": 1.59 * mm});
            skCircle(sketch, "E47.8.0.0", {"center": v(295.76, 4.3) * mm, "radius": 1.59 * mm});
            skCircle(sketch, "E47.8.1.0", {"center": v(295.76, 10.64) * mm, "radius": 1.59 * mm});
            skCircle(sketch, "E47.8.2.0", {"center": v(295.76, 17) * mm, "radius": 1.59 * mm});
            skCircle(sketch, "E47.8.3.0", {"center": v(295.76, 23.34) * mm, "radius": 1.59 * mm});
            skCircle(sketch, "E47.8.4.0", {"center": v(295.76, 29.7) * mm, "radius": 1.59 * mm});
            skCircle(sketch, "E47.8.5.0", {"center": v(295.76, 36.04) * mm, "radius": 1.59 * mm});
            skCircle(sketch, "E47.8.6.0", {"center": v(295.76, 42.4) * mm, "radius": 1.59 * mm});
            skCircle(sketch, "E47.8.7.0", {"center": v(295.76, 48.74) * mm, "radius": 1.59 * mm});
            skCircle(sketch, "E47.8.8.0", {"center": v(295.76, 55.1) * mm, "radius": 1.59 * mm});
            skCircle(sketch, "E47.8.9.0", {"center": v(295.76, 61.44) * mm, "radius": 1.59 * mm});
            skCircle(sketch, "E47.8.10.0", {"center": v(295.76, 67.8) * mm, "radius": 1.59 * mm});
            skCircle(sketch, "E47.8.11.0", {"center": v(295.76, 74.14) * mm, "radius": 1.59 * mm});
            skCircle(sketch, "E47.8.12.0", {"center": v(295.76, 80.5) * mm, "radius": 1.59 * mm});
            skCircle(sketch, "E47.8.13.0", {"center": v(295.76, 86.84) * mm, "radius": 1.59 * mm});
            skCircle(sketch, "E47.8.14.0", {"center": v(295.76, 93.2) * mm, "radius": 1.59 * mm});
            skCircle(sketch, "E47.8.15.0", {"center": v(295.76, 99.54) * mm, "radius": 1.59 * mm});
            skCircle(sketch, "E47.8.16.0", {"center": v(295.76, 105.9) * mm, "radius": 1.59 * mm});
            skCircle(sketch, "E47.9.0.0", {"center": v(302.1, 4.3) * mm, "radius": 1.59 * mm});
            skCircle(sketch, "E47.9.1.0", {"center": v(302.1, 10.64) * mm, "radius": 1.59 * mm});
            skCircle(sketch, "E47.9.2.0", {"center": v(302.1, 17) * mm, "radius": 1.59 * mm});
            skCircle(sketch, "E47.9.3.0", {"center": v(302.1, 23.34) * mm, "radius": 1.59 * mm});
            skCircle(sketch, "E47.9.4.0", {"center": v(302.1, 29.7) * mm, "radius": 1.59 * mm});
            skCircle(sketch, "E47.9.5.0", {"center": v(302.1, 36.04) * mm, "radius": 1.59 * mm});
            skCircle(sketch, "E47.9.6.0", {"center": v(302.1, 42.4) * mm, "radius": 1.59 * mm});
            skCircle(sketch, "E47.9.7.0", {"center": v(302.1, 48.74) * mm, "radius": 1.59 * mm});
            skCircle(sketch, "E47.9.8.0", {"center": v(302.1, 55.1) * mm, "radius": 1.59 * mm});
            skCircle(sketch, "E47.9.9.0", {"center": v(302.1, 61.44) * mm, "radius": 1.59 * mm});
            skCircle(sketch, "E47.9.10.0", {"center": v(302.1, 67.8) * mm, "radius": 1.59 * mm});
            skCircle(sketch, "E47.9.11.0", {"center": v(302.1, 74.14) * mm, "radius": 1.59 * mm});
            skCircle(sketch, "E47.9.12.0", {"center": v(302.1, 80.5) * mm, "radius": 1.59 * mm});
            skCircle(sketch, "E47.9.13.0", {"center": v(302.1, 86.84) * mm, "radius": 1.59 * mm});
            skCircle(sketch, "E47.9.14.0", {"center": v(302.1, 93.2) * mm, "radius": 1.59 * mm});
            skCircle(sketch, "E47.9.15.0", {"center": v(302.1, 99.54) * mm, "radius": 1.59 * mm});
            skCircle(sketch, "E47.9.16.0", {"center": v(302.1, 105.9) * mm, "radius": 1.59 * mm});
            skCircle(sketch, "E47.10.0.0", {"center": v(308.46, 4.3) * mm, "radius": 1.59 * mm});
            skCircle(sketch, "E47.10.1.0", {"center": v(308.46, 10.64) * mm, "radius": 1.59 * mm});
            skCircle(sketch, "E47.10.2.0", {"center": v(308.46, 17) * mm, "radius": 1.59 * mm});
            skCircle(sketch, "E47.10.3.0", {"center": v(308.46, 23.34) * mm, "radius": 1.59 * mm});
            skCircle(sketch, "E47.10.4.0", {"center": v(308.46, 29.7) * mm, "radius": 1.59 * mm});
            skCircle(sketch, "E47.10.5.0", {"center": v(308.46, 36.04) * mm, "radius": 1.59 * mm});
            skCircle(sketch, "E47.10.6.0", {"center": v(308.46, 42.4) * mm, "radius": 1.59 * mm});
            skCircle(sketch, "E47.10.7.0", {"center": v(308.46, 48.74) * mm, "radius": 1.59 * mm});
            skCircle(sketch, "E47.10.8.0", {"center": v(308.46, 55.1) * mm, "radius": 1.59 * mm});
            skCircle(sketch, "E47.10.9.0", {"center": v(308.46, 61.44) * mm, "radius": 1.59 * mm});
            skCircle(sketch, "E47.10.10.0", {"center": v(308.46, 67.8) * mm, "radius": 1.59 * mm});
            skCircle(sketch, "E47.10.11.0", {"center": v(308.46, 74.14) * mm, "radius": 1.59 * mm});
            skCircle(sketch, "E47.10.12.0", {"center": v(308.46, 80.5) * mm, "radius": 1.59 * mm});
            skCircle(sketch, "E47.10.13.0", {"center": v(308.46, 86.84) * mm, "radius": 1.59 * mm});
            skCircle(sketch, "E47.10.14.0", {"center": v(308.46, 93.2) * mm, "radius": 1.59 * mm});
            skCircle(sketch, "E47.10.15.0", {"center": v(308.46, 99.54) * mm, "radius": 1.59 * mm});
            skCircle(sketch, "E47.10.16.0", {"center": v(308.46, 105.9) * mm, "radius": 1.59 * mm});
            skCircle(sketch, "E47.11.0.0", {"center": v(314.8, 4.3) * mm, "radius": 1.59 * mm});
            skCircle(sketch, "E47.11.1.0", {"center": v(314.8, 10.64) * mm, "radius": 1.59 * mm});
            skCircle(sketch, "E47.11.2.0", {"center": v(314.8, 17) * mm, "radius": 1.59 * mm});
            skCircle(sketch, "E47.11.3.0", {"center": v(314.8, 23.34) * mm, "radius": 1.59 * mm});
            skCircle(sketch, "E47.11.4.0", {"center": v(314.8, 29.7) * mm, "radius": 1.59 * mm});
            skCircle(sketch, "E47.11.5.0", {"center": v(314.8, 36.04) * mm, "radius": 1.59 * mm});
            skCircle(sketch, "E47.11.6.0", {"center": v(314.8, 42.4) * mm, "radius": 1.59 * mm});
            skCircle(sketch, "E47.11.7.0", {"center": v(314.8, 48.74) * mm, "radius": 1.59 * mm});
            skCircle(sketch, "E47.11.8.0", {"center": v(314.8, 55.1) * mm, "radius": 1.59 * mm});
            skCircle(sketch, "E47.11.9.0", {"center": v(314.8, 61.44) * mm, "radius": 1.59 * mm});
            skCircle(sketch, "E47.11.10.0", {"center": v(314.8, 67.8) * mm, "radius": 1.59 * mm});
            skCircle(sketch, "E47.11.11.0", {"center": v(314.8, 74.14) * mm, "radius": 1.59 * mm});
            skCircle(sketch, "E47.11.12.0", {"center": v(314.8, 80.5) * mm, "radius": 1.59 * mm});
            skCircle(sketch, "E47.11.13.0", {"center": v(314.8, 86.84) * mm, "radius": 1.59 * mm});
            skCircle(sketch, "E47.11.14.0", {"center": v(314.8, 93.2) * mm, "radius": 1.59 * mm});
            skCircle(sketch, "E47.11.15.0", {"center": v(314.8, 99.54) * mm, "radius": 1.59 * mm});
            skCircle(sketch, "E47.11.16.0", {"center": v(314.8, 105.9) * mm, "radius": 1.59 * mm});
            skCircle(sketch, "E47.12.0.0", {"center": v(321.16, 4.3) * mm, "radius": 1.59 * mm});
            skCircle(sketch, "E47.12.1.0", {"center": v(321.16, 10.64) * mm, "radius": 1.59 * mm});
            skCircle(sketch, "E47.12.2.0", {"center": v(321.16, 17) * mm, "radius": 1.59 * mm});
            skCircle(sketch, "E47.12.3.0", {"center": v(321.16, 23.34) * mm, "radius": 1.59 * mm});
            skCircle(sketch, "E47.12.4.0", {"center": v(321.16, 29.7) * mm, "radius": 1.59 * mm});
            skCircle(sketch, "E47.12.5.0", {"center": v(321.16, 36.04) * mm, "radius": 1.59 * mm});
            skCircle(sketch, "E47.12.6.0", {"center": v(321.16, 42.4) * mm, "radius": 1.59 * mm});
            skCircle(sketch, "E47.12.7.0", {"center": v(321.16, 48.74) * mm, "radius": 1.59 * mm});
            skCircle(sketch, "E47.12.8.0", {"center": v(321.16, 55.1) * mm, "radius": 1.59 * mm});
            skCircle(sketch, "E47.12.9.0", {"center": v(321.16, 61.44) * mm, "radius": 1.59 * mm});
            skCircle(sketch, "E47.12.10.0", {"center": v(321.16, 67.8) * mm, "radius": 1.59 * mm});
            skCircle(sketch, "E47.12.11.0", {"center": v(321.16, 74.14) * mm, "radius": 1.59 * mm});
            skCircle(sketch, "E47.12.12.0", {"center": v(321.16, 80.5) * mm, "radius": 1.59 * mm});
            skCircle(sketch, "E47.12.13.0", {"center": v(321.16, 86.84) * mm, "radius": 1.59 * mm});
            skCircle(sketch, "E47.12.14.0", {"center": v(321.16, 93.2) * mm, "radius": 1.59 * mm});
            skCircle(sketch, "E47.12.15.0", {"center": v(321.16, 99.54) * mm, "radius": 1.59 * mm});
            skCircle(sketch, "E47.12.16.0", {"center": v(321.16, 105.9) * mm, "radius": 1.59 * mm});
            skCircle(sketch, "E47.13.0.0", {"center": v(327.5, 4.3) * mm, "radius": 1.59 * mm});
            skCircle(sketch, "E47.13.1.0", {"center": v(327.5, 10.64) * mm, "radius": 1.59 * mm});
            skCircle(sketch, "E47.13.2.0", {"center": v(327.5, 17) * mm, "radius": 1.59 * mm});
            skCircle(sketch, "E47.13.3.0", {"center": v(327.5, 23.34) * mm, "radius": 1.59 * mm});
            skCircle(sketch, "E47.13.4.0", {"center": v(327.5, 29.7) * mm, "radius": 1.59 * mm});
            skCircle(sketch, "E47.13.5.0", {"center": v(327.5, 36.04) * mm, "radius": 1.59 * mm});
            skCircle(sketch, "E47.13.6.0", {"center": v(327.5, 42.4) * mm, "radius": 1.59 * mm});
            skCircle(sketch, "E47.13.7.0", {"center": v(327.5, 48.74) * mm, "radius": 1.59 * mm});
            skCircle(sketch, "E47.13.8.0", {"center": v(327.5, 55.1) * mm, "radius": 1.59 * mm});
            skCircle(sketch, "E47.13.9.0", {"center": v(327.5, 61.44) * mm, "radius": 1.59 * mm});
            skCircle(sketch, "E47.13.10.0", {"center": v(327.5, 67.8) * mm, "radius": 1.59 * mm});
            skCircle(sketch, "E47.13.11.0", {"center": v(327.5, 74.14) * mm, "radius": 1.59 * mm});
            skCircle(sketch, "E47.13.12.0", {"center": v(327.5, 80.5) * mm, "radius": 1.59 * mm});
            skCircle(sketch, "E47.13.13.0", {"center": v(327.5, 86.84) * mm, "radius": 1.59 * mm});
            skCircle(sketch, "E47.13.14.0", {"center": v(327.5, 93.2) * mm, "radius": 1.59 * mm});
            skCircle(sketch, "E47.13.15.0", {"center": v(327.5, 99.54) * mm, "radius": 1.59 * mm});
            skCircle(sketch, "E47.13.16.0", {"center": v(327.5, 105.9) * mm, "radius": 1.59 * mm});
            skCircle(sketch, "E47.14.0.0", {"center": v(333.86, 4.3) * mm, "radius": 1.59 * mm});
            skCircle(sketch, "E47.14.1.0", {"center": v(333.86, 10.64) * mm, "radius": 1.59 * mm});
            skCircle(sketch, "E47.14.2.0", {"center": v(333.86, 17) * mm, "radius": 1.59 * mm});
            skCircle(sketch, "E47.14.3.0", {"center": v(333.86, 23.34) * mm, "radius": 1.59 * mm});
            skCircle(sketch, "E47.14.4.0", {"center": v(333.86, 29.7) * mm, "radius": 1.59 * mm});
            skCircle(sketch, "E47.14.5.0", {"center": v(333.86, 36.04) * mm, "radius": 1.59 * mm});
            skCircle(sketch, "E47.14.6.0", {"center": v(333.86, 42.4) * mm, "radius": 1.59 * mm});
            skCircle(sketch, "E47.14.7.0", {"center": v(333.86, 48.74) * mm, "radius": 1.59 * mm});
            skCircle(sketch, "E47.14.8.0", {"center": v(333.86, 55.1) * mm, "radius": 1.59 * mm});
            skCircle(sketch, "E47.14.9.0", {"center": v(333.86, 61.44) * mm, "radius": 1.59 * mm});
            skCircle(sketch, "E47.14.10.0", {"center": v(333.86, 67.8) * mm, "radius": 1.59 * mm});
            skCircle(sketch, "E47.14.11.0", {"center": v(333.86, 74.14) * mm, "radius": 1.59 * mm});
            skCircle(sketch, "E47.14.12.0", {"center": v(333.86, 80.5) * mm, "radius": 1.59 * mm});
            skCircle(sketch, "E47.14.13.0", {"center": v(333.86, 86.84) * mm, "radius": 1.59 * mm});
            skCircle(sketch, "E47.14.14.0", {"center": v(333.86, 93.2) * mm, "radius": 1.59 * mm});
            skCircle(sketch, "E47.14.15.0", {"center": v(333.86, 99.54) * mm, "radius": 1.59 * mm});
            skCircle(sketch, "E47.14.16.0", {"center": v(333.86, 105.9) * mm, "radius": 1.59 * mm});
            skCircle(sketch, "E47.15.0.0", {"center": v(340.2, 4.3) * mm, "radius": 1.59 * mm});
            skCircle(sketch, "E47.15.1.0", {"center": v(340.2, 10.64) * mm, "radius": 1.59 * mm});
            skCircle(sketch, "E47.15.2.0", {"center": v(340.2, 17) * mm, "radius": 1.59 * mm});
            skCircle(sketch, "E47.15.3.0", {"center": v(340.2, 23.34) * mm, "radius": 1.59 * mm});
            skCircle(sketch, "E47.15.4.0", {"center": v(340.2, 29.7) * mm, "radius": 1.59 * mm});
            skCircle(sketch, "E47.15.5.0", {"center": v(340.2, 36.04) * mm, "radius": 1.59 * mm});
            skCircle(sketch, "E47.15.6.0", {"center": v(340.2, 42.4) * mm, "radius": 1.59 * mm});
            skCircle(sketch, "E47.15.7.0", {"center": v(340.2, 48.74) * mm, "radius": 1.59 * mm});
            skCircle(sketch, "E47.15.8.0", {"center": v(340.2, 55.1) * mm, "radius": 1.59 * mm});
            skCircle(sketch, "E47.15.9.0", {"center": v(340.2, 61.44) * mm, "radius": 1.59 * mm});
            skCircle(sketch, "E47.15.10.0", {"center": v(340.2, 67.8) * mm, "radius": 1.59 * mm});
            skCircle(sketch, "E47.15.11.0", {"center": v(340.2, 74.14) * mm, "radius": 1.59 * mm});
            skCircle(sketch, "E47.15.12.0", {"center": v(340.2, 80.5) * mm, "radius": 1.59 * mm});
            skCircle(sketch, "E47.15.13.0", {"center": v(340.2, 86.84) * mm, "radius": 1.59 * mm});
            skCircle(sketch, "E47.15.14.0", {"center": v(340.2, 93.2) * mm, "radius": 1.59 * mm});
            skCircle(sketch, "E47.15.15.0", {"center": v(340.2, 99.54) * mm, "radius": 1.59 * mm});
            skCircle(sketch, "E47.15.16.0", {"center": v(340.2, 105.9) * mm, "radius": 1.59 * mm});
            skCircle(sketch, "E47.16.0.0", {"center": v(346.56, 4.3) * mm, "radius": 1.59 * mm});
            skCircle(sketch, "E47.16.1.0", {"center": v(346.56, 10.64) * mm, "radius": 1.59 * mm});
            skCircle(sketch, "E47.16.2.0", {"center": v(346.56, 17) * mm, "radius": 1.59 * mm});
            skCircle(sketch, "E47.16.3.0", {"center": v(346.56, 23.34) * mm, "radius": 1.59 * mm});
            skCircle(sketch, "E47.16.4.0", {"center": v(346.56, 29.7) * mm, "radius": 1.59 * mm});
            skCircle(sketch, "E47.16.5.0", {"center": v(346.56, 36.04) * mm, "radius": 1.59 * mm});
            skCircle(sketch, "E47.16.6.0", {"center": v(346.56, 42.4) * mm, "radius": 1.59 * mm});
            skCircle(sketch, "E47.16.7.0", {"center": v(346.56, 48.74) * mm, "radius": 1.59 * mm});
            skCircle(sketch, "E47.16.8.0", {"center": v(346.56, 55.1) * mm, "radius": 1.59 * mm});
            skCircle(sketch, "E47.16.9.0", {"center": v(346.56, 61.44) * mm, "radius": 1.59 * mm});
            skCircle(sketch, "E47.16.10.0", {"center": v(346.56, 67.8) * mm, "radius": 1.59 * mm});
            skCircle(sketch, "E47.16.11.0", {"center": v(346.56, 74.14) * mm, "radius": 1.59 * mm});
            skCircle(sketch, "E47.16.12.0", {"center": v(346.56, 80.5) * mm, "radius": 1.59 * mm});
            skCircle(sketch, "E47.16.13.0", {"center": v(346.56, 86.84) * mm, "radius": 1.59 * mm});
            skCircle(sketch, "E47.16.14.0", {"center": v(346.56, 93.2) * mm, "radius": 1.59 * mm});
            skCircle(sketch, "E47.16.15.0", {"center": v(346.56, 99.54) * mm, "radius": 1.59 * mm});
            skCircle(sketch, "E47.16.16.0", {"center": v(346.56, 105.9) * mm, "radius": 1.59 * mm});
            skLineSegment(sketch, "E47.direction1", {"start": v(244.96, 4.3) * mm, "end": v(251.3, 4.3) * mm, "construction": true});
            skLineSegment(sketch, "E47.direction2", {"start": v(244.96, 4.3) * mm, "end": v(244.96, 10.64) * mm, "construction": true});
            skLineSegment(sketch, "E48", {"start": v(450.72, 112.24) * mm, "end": v(457.07, 112.24) * mm, "construction": true});
            skLineSegment(sketch, "E49", {"start": v(453.9, 112.24) * mm, "end": v(453.9, 10.64) * mm, "construction": true});
            skCircle(sketch, "E50.MirrorC", {"center": v(662.84, 4.3) * mm, "radius": 1.59 * mm});
            skCircle(sketch, "E51.MirrorC", {"center": v(561.24, 105.9) * mm, "radius": 1.59 * mm});
            skCircle(sketch, "E52.MirrorC", {"center": v(662.84, 105.9) * mm, "radius": 1.59 * mm});
            skCircle(sketch, "E53.MirrorC", {"center": v(561.24, 4.3) * mm, "radius": 1.59 * mm});
            skCircle(sketch, "E54.MirrorC", {"center": v(656.49, 4.3) * mm, "radius": 1.59 * mm});
            skLineSegment(sketch, "E55.MirrorCS", {"start": v(662.84, 4.3) * mm, "end": v(662.84, 10.64) * mm, "construction": true});
            skCircle(sketch, "E56.MirrorC", {"center": v(662.84, 10.64) * mm, "radius": 1.59 * mm});
            skLineSegment(sketch, "E57.MirrorCS", {"start": v(662.84, 4.3) * mm, "end": v(656.49, 4.3) * mm, "construction": true});
            skCircle(sketch, "E58.MirrorC", {"center": v(612.04, 48.74) * mm, "radius": 1.59 * mm});
            skCircle(sketch, "E59.MirrorC", {"center": v(618.39, 10.64) * mm, "radius": 1.59 * mm});
            skCircle(sketch, "E60.MirrorC", {"center": v(618.39, 99.54) * mm, "radius": 1.59 * mm});
            skCircle(sketch, "E61.MirrorC", {"center": v(618.39, 55.1) * mm, "radius": 1.59 * mm});
            skCircle(sketch, "E62.MirrorC", {"center": v(567.59, 17) * mm, "radius": 1.59 * mm});
            skCircle(sketch, "E63.MirrorC", {"center": v(650.14, 61.44) * mm, "radius": 1.59 * mm});
            skCircle(sketch, "E64.MirrorC", {"center": v(586.64, 80.5) * mm, "radius": 1.59 * mm});
            skLineSegment(sketch, "E65.MirrorCS", {"start": v(662.84, 105.9) * mm, "end": v(662.84, 4.3) * mm, "construction": true});
            skCircle(sketch, "E66.MirrorC", {"center": v(618.39, 105.9) * mm, "radius": 1.59 * mm});
            skCircle(sketch, "E67.MirrorC", {"center": v(599.34, 93.2) * mm, "radius": 1.59 * mm});
            skCircle(sketch, "E68.MirrorC", {"center": v(605.69, 74.14) * mm, "radius": 1.59 * mm});
            skCircle(sketch, "E69.MirrorC", {"center": v(573.94, 93.2) * mm, "radius": 1.59 * mm});
            skCircle(sketch, "E70.MirrorC", {"center": v(573.94, 67.8) * mm, "radius": 1.59 * mm});
            skCircle(sketch, "E71.MirrorC", {"center": v(599.34, 10.64) * mm, "radius": 1.59 * mm});
            skCircle(sketch, "E72.MirrorC", {"center": v(643.79, 4.3) * mm, "radius": 1.59 * mm});
            skCircle(sketch, "E73.MirrorC", {"center": v(567.59, 42.4) * mm, "radius": 1.59 * mm});
            skCircle(sketch, "E74.MirrorC", {"center": v(656.49, 99.54) * mm, "radius": 1.59 * mm});
            skCircle(sketch, "E75.MirrorC", {"center": v(656.49, 42.4) * mm, "radius": 1.59 * mm});
            skCircle(sketch, "E76.MirrorC", {"center": v(643.79, 86.84) * mm, "radius": 1.59 * mm});
            skCircle(sketch, "E77.MirrorC", {"center": v(662.84, 86.84) * mm, "radius": 1.59 * mm});
            skCircle(sketch, "E78.MirrorC", {"center": v(662.84, 74.14) * mm, "radius": 1.59 * mm});
            skCircle(sketch, "E79.MirrorC", {"center": v(650.14, 36.04) * mm, "radius": 1.59 * mm});
            skCircle(sketch, "E80.MirrorC", {"center": v(637.44, 17) * mm, "radius": 1.59 * mm});
            skCircle(sketch, "E81.MirrorC", {"center": v(624.74, 36.04) * mm, "radius": 1.59 * mm});
            skCircle(sketch, "E82.MirrorC", {"center": v(662.84, 23.34) * mm, "radius": 1.59 * mm});
            skCircle(sketch, "E83.MirrorC", {"center": v(592.99, 29.7) * mm, "radius": 1.59 * mm});
            skCircle(sketch, "E84.MirrorC", {"center": v(618.39, 93.2) * mm, "radius": 1.59 * mm});
            skCircle(sketch, "E85.MirrorC", {"center": v(624.74, 61.44) * mm, "radius": 1.59 * mm});
            skCircle(sketch, "E86.MirrorC", {"center": v(592.99, 61.44) * mm, "radius": 1.59 * mm});
            skCircle(sketch, "E87.MirrorC", {"center": v(612.04, 80.5) * mm, "radius": 1.59 * mm});
            skCircle(sketch, "E88.MirrorC", {"center": v(586.64, 55.1) * mm, "radius": 1.59 * mm});
            skCircle(sketch, "E89.MirrorC", {"center": v(605.69, 105.9) * mm, "radius": 1.59 * mm});
            skCircle(sketch, "E90.MirrorC", {"center": v(612.04, 36.04) * mm, "radius": 1.59 * mm});
            skCircle(sketch, "E91.MirrorC", {"center": v(561.24, 86.84) * mm, "radius": 1.59 * mm});
            skCircle(sketch, "E92.MirrorC", {"center": v(599.34, 17) * mm, "radius": 1.59 * mm});
            skCircle(sketch, "E93.MirrorC", {"center": v(624.74, 42.4) * mm, "radius": 1.59 * mm});
            skCircle(sketch, "E94.MirrorC", {"center": v(561.24, 67.8) * mm, "radius": 1.59 * mm});
            skCircle(sketch, "E95.MirrorC", {"center": v(637.44, 80.5) * mm, "radius": 1.59 * mm});
            skCircle(sketch, "E96.MirrorC", {"center": v(637.44, 36.04) * mm, "radius": 1.59 * mm});
            skCircle(sketch, "E97.MirrorC", {"center": v(561.24, 17) * mm, "radius": 1.59 * mm});
            skCircle(sketch, "E98.MirrorC", {"center": v(656.49, 10.64) * mm, "radius": 1.59 * mm});
            skCircle(sketch, "E99.MirrorC", {"center": v(605.69, 23.34) * mm, "radius": 1.59 * mm});
            skCircle(sketch, "E100.MirrorC", {"center": v(580.29, 17) * mm, "radius": 1.59 * mm});
            skCircle(sketch, "E101.MirrorC", {"center": v(599.34, 67.8) * mm, "radius": 1.59 * mm});
            skCircle(sketch, "E102.MirrorC", {"center": v(656.49, 80.5) * mm, "radius": 1.59 * mm});
            skCircle(sketch, "E103.MirrorC", {"center": v(573.94, 74.14) * mm, "radius": 1.59 * mm});
            skCircle(sketch, "E104.MirrorC", {"center": v(650.14, 74.14) * mm, "radius": 1.59 * mm});
            skCircle(sketch, "E105.MirrorC", {"center": v(567.59, 10.64) * mm, "radius": 1.59 * mm});
            skCircle(sketch, "E106.MirrorC", {"center": v(650.14, 42.4) * mm, "radius": 1.59 * mm});
            skCircle(sketch, "E107.MirrorC", {"center": v(586.64, 48.74) * mm, "radius": 1.59 * mm});
            skCircle(sketch, "E108.MirrorC", {"center": v(618.39, 48.74) * mm, "radius": 1.59 * mm});
            skCircle(sketch, "E109.MirrorC", {"center": v(656.49, 67.8) * mm, "radius": 1.59 * mm});
            skCircle(sketch, "E110.MirrorC", {"center": v(567.59, 36.04) * mm, "radius": 1.59 * mm});
            skCircle(sketch, "E111.MirrorC", {"center": v(624.74, 23.34) * mm, "radius": 1.59 * mm});
            skCircle(sketch, "E112.MirrorC", {"center": v(567.59, 23.34) * mm, "radius": 1.59 * mm});
            skCircle(sketch, "E113.MirrorC", {"center": v(618.39, 4.3) * mm, "radius": 1.59 * mm});
            skCircle(sketch, "E114.MirrorC", {"center": v(637.44, 99.54) * mm, "radius": 1.59 * mm});
            skCircle(sketch, "E115.MirrorC", {"center": v(592.99, 93.2) * mm, "radius": 1.59 * mm});
            skCircle(sketch, "E116.MirrorC", {"center": v(561.24, 48.74) * mm, "radius": 1.59 * mm});
            skCircle(sketch, "E117.MirrorC", {"center": v(637.44, 61.44) * mm, "radius": 1.59 * mm});
            skCircle(sketch, "E118.MirrorC", {"center": v(567.59, 29.7) * mm, "radius": 1.59 * mm});
            skCircle(sketch, "E119.MirrorC", {"center": v(592.99, 23.34) * mm, "radius": 1.59 * mm});
            skCircle(sketch, "E120.MirrorC", {"center": v(650.14, 23.34) * mm, "radius": 1.59 * mm});
            skCircle(sketch, "E121.MirrorC", {"center": v(631.09, 36.04) * mm, "radius": 1.59 * mm});
            skCircle(sketch, "E122.MirrorC", {"center": v(580.29, 80.5) * mm, "radius": 1.59 * mm});
            skCircle(sketch, "E123.MirrorC", {"center": v(605.69, 4.3) * mm, "radius": 1.59 * mm});
            skCircle(sketch, "E124.MirrorC", {"center": v(631.09, 17) * mm, "radius": 1.59 * mm});
            skCircle(sketch, "E125.MirrorC", {"center": v(650.14, 17) * mm, "radius": 1.59 * mm});
            skCircle(sketch, "E126.MirrorC", {"center": v(605.69, 10.64) * mm, "radius": 1.59 * mm});
            skCircle(sketch, "E127.MirrorC", {"center": v(592.99, 74.14) * mm, "radius": 1.59 * mm});
            skCircle(sketch, "E128.MirrorC", {"center": v(605.69, 61.44) * mm, "radius": 1.59 * mm});
            skCircle(sketch, "E129.MirrorC", {"center": v(637.44, 10.64) * mm, "radius": 1.59 * mm});
            skCircle(sketch, "E130.MirrorC", {"center": v(586.64, 42.4) * mm, "radius": 1.59 * mm});
            skCircle(sketch, "E131.MirrorC", {"center": v(580.29, 10.64) * mm, "radius": 1.59 * mm});
            skCircle(sketch, "E132.MirrorC", {"center": v(561.24, 10.64) * mm, "radius": 1.59 * mm});
            skCircle(sketch, "E133.MirrorC", {"center": v(643.79, 93.2) * mm, "radius": 1.59 * mm});
            skCircle(sketch, "E134.MirrorC", {"center": v(573.94, 86.84) * mm, "radius": 1.59 * mm});
            skCircle(sketch, "E135.MirrorC", {"center": v(561.24, 23.34) * mm, "radius": 1.59 * mm});
            skCircle(sketch, "E136.MirrorC", {"center": v(618.39, 36.04) * mm, "radius": 1.59 * mm});
            skCircle(sketch, "E137.MirrorC", {"center": v(573.94, 42.4) * mm, "radius": 1.59 * mm});
            skCircle(sketch, "E138.MirrorC", {"center": v(631.09, 105.9) * mm, "radius": 1.59 * mm});
            skCircle(sketch, "E139.MirrorC", {"center": v(631.09, 29.7) * mm, "radius": 1.59 * mm});
            skCircle(sketch, "E140.MirrorC", {"center": v(643.79, 61.44) * mm, "radius": 1.59 * mm});
            skCircle(sketch, "E141.MirrorC", {"center": v(612.04, 74.14) * mm, "radius": 1.59 * mm});
            skCircle(sketch, "E142.MirrorC", {"center": v(599.34, 80.5) * mm, "radius": 1.59 * mm});
            skCircle(sketch, "E143.MirrorC", {"center": v(631.09, 61.44) * mm, "radius": 1.59 * mm});
            skCircle(sketch, "E144.MirrorC", {"center": v(618.39, 23.34) * mm, "radius": 1.59 * mm});
            skCircle(sketch, "E145.MirrorC", {"center": v(580.29, 36.04) * mm, "radius": 1.59 * mm});
            skCircle(sketch, "E146.MirrorC", {"center": v(656.49, 36.04) * mm, "radius": 1.59 * mm});
            skCircle(sketch, "E147.MirrorC", {"center": v(662.84, 36.04) * mm, "radius": 1.59 * mm});
            skCircle(sketch, "E148.MirrorC", {"center": v(643.79, 48.74) * mm, "radius": 1.59 * mm});
            skCircle(sketch, "E149.MirrorC", {"center": v(662.84, 48.74) * mm, "radius": 1.59 * mm});
            skCircle(sketch, "E150.MirrorC", {"center": v(599.34, 42.4) * mm, "radius": 1.59 * mm});
            skCircle(sketch, "E151.MirrorC", {"center": v(650.14, 29.7) * mm, "radius": 1.59 * mm});
            skLineSegment(sketch, "E152.MirrorCS", {"start": v(662.84, 105.9) * mm, "end": v(561.11, 105.9) * mm, "construction": true});
            skCircle(sketch, "E153.MirrorC", {"center": v(586.64, 10.64) * mm, "radius": 1.59 * mm});
            skCircle(sketch, "E154.MirrorC", {"center": v(631.09, 67.8) * mm, "radius": 1.59 * mm});
            skLineSegment(sketch, "E155.MirrorCS", {"start": v(662.84, 4.3) * mm, "end": v(561.11, 4.3) * mm, "construction": true});
            skCircle(sketch, "E156.MirrorC", {"center": v(605.69, 55.1) * mm, "radius": 1.59 * mm});
            skCircle(sketch, "E157.MirrorC", {"center": v(580.29, 86.84) * mm, "radius": 1.59 * mm});
            skCircle(sketch, "E158.MirrorC", {"center": v(599.34, 4.3) * mm, "radius": 1.59 * mm});
            skCircle(sketch, "E159.MirrorC", {"center": v(592.99, 67.8) * mm, "radius": 1.59 * mm});
            skCircle(sketch, "E160.MirrorC", {"center": v(643.79, 105.9) * mm, "radius": 1.59 * mm});
            skCircle(sketch, "E161.MirrorC", {"center": v(580.29, 105.9) * mm, "radius": 1.59 * mm});
            skCircle(sketch, "E162.MirrorC", {"center": v(573.94, 99.54) * mm, "radius": 1.59 * mm});
            skCircle(sketch, "E163.MirrorC", {"center": v(561.24, 93.2) * mm, "radius": 1.59 * mm});
            skLineSegment(sketch, "E164.MirrorCS", {"start": v(561.11, 105.9) * mm, "end": v(561.11, 4.3) * mm, "construction": true});
            skCircle(sketch, "E165.MirrorC", {"center": v(580.29, 23.34) * mm, "radius": 1.59 * mm});
            skCircle(sketch, "E166.MirrorC", {"center": v(573.94, 17) * mm, "radius": 1.59 * mm});
            skCircle(sketch, "E167.MirrorC", {"center": v(650.14, 99.54) * mm, "radius": 1.59 * mm});
            skCircle(sketch, "E168.MirrorC", {"center": v(650.14, 4.3) * mm, "radius": 1.59 * mm});
            skCircle(sketch, "E169.MirrorC", {"center": v(586.64, 93.2) * mm, "radius": 1.59 * mm});
            skCircle(sketch, "E170.MirrorC", {"center": v(662.84, 42.4) * mm, "radius": 1.59 * mm});
            skCircle(sketch, "E171.MirrorC", {"center": v(631.09, 23.34) * mm, "radius": 1.59 * mm});
            skCircle(sketch, "E172.MirrorC", {"center": v(618.39, 67.8) * mm, "radius": 1.59 * mm});
            skCircle(sketch, "E173.MirrorC", {"center": v(592.99, 99.54) * mm, "radius": 1.59 * mm});
            skCircle(sketch, "E174.MirrorC", {"center": v(643.79, 17) * mm, "radius": 1.59 * mm});
            skCircle(sketch, "E175.MirrorC", {"center": v(631.09, 48.74) * mm, "radius": 1.59 * mm});
            skCircle(sketch, "E176.MirrorC", {"center": v(643.79, 36.04) * mm, "radius": 1.59 * mm});
            skCircle(sketch, "E177.MirrorC", {"center": v(612.04, 86.84) * mm, "radius": 1.59 * mm});
            skCircle(sketch, "E178.MirrorC", {"center": v(637.44, 86.84) * mm, "radius": 1.59 * mm});
            skCircle(sketch, "E179.MirrorC", {"center": v(612.04, 99.54) * mm, "radius": 1.59 * mm});
            skCircle(sketch, "E180.MirrorC", {"center": v(605.69, 42.4) * mm, "radius": 1.59 * mm});
            skCircle(sketch, "E181.MirrorC", {"center": v(624.74, 93.2) * mm, "radius": 1.59 * mm});
            skCircle(sketch, "E182.MirrorC", {"center": v(567.59, 67.8) * mm, "radius": 1.59 * mm});
            skCircle(sketch, "E183.MirrorC", {"center": v(605.69, 48.74) * mm, "radius": 1.59 * mm});
            skCircle(sketch, "E184.MirrorC", {"center": v(573.94, 29.7) * mm, "radius": 1.59 * mm});
            skCircle(sketch, "E185.MirrorC", {"center": v(561.24, 74.14) * mm, "radius": 1.59 * mm});
            skCircle(sketch, "E186.MirrorC", {"center": v(637.44, 23.34) * mm, "radius": 1.59 * mm});
            skCircle(sketch, "E187.MirrorC", {"center": v(637.44, 29.7) * mm, "radius": 1.59 * mm});
            skCircle(sketch, "E188.MirrorC", {"center": v(624.74, 86.84) * mm, "radius": 1.59 * mm});
            skCircle(sketch, "E189.MirrorC", {"center": v(580.29, 67.8) * mm, "radius": 1.59 * mm});
            skCircle(sketch, "E190.MirrorC", {"center": v(586.64, 105.9) * mm, "radius": 1.59 * mm});
            skCircle(sketch, "E191.MirrorC", {"center": v(586.64, 17) * mm, "radius": 1.59 * mm});
            skCircle(sketch, "E192.MirrorC", {"center": v(662.84, 80.5) * mm, "radius": 1.59 * mm});
            skCircle(sketch, "E193.MirrorC", {"center": v(580.29, 42.4) * mm, "radius": 1.59 * mm});
            skCircle(sketch, "E194.MirrorC", {"center": v(592.99, 10.64) * mm, "radius": 1.59 * mm});
            skCircle(sketch, "E195.MirrorC", {"center": v(618.39, 86.84) * mm, "radius": 1.59 * mm});
            skCircle(sketch, "E196.MirrorC", {"center": v(561.24, 42.4) * mm, "radius": 1.59 * mm});
            skCircle(sketch, "E197.MirrorC", {"center": v(567.59, 105.9) * mm, "radius": 1.59 * mm});
            skCircle(sketch, "E198.MirrorC", {"center": v(643.79, 55.1) * mm, "radius": 1.59 * mm});
            skCircle(sketch, "E199.MirrorC", {"center": v(592.99, 55.1) * mm, "radius": 1.59 * mm});
            skCircle(sketch, "E200.MirrorC", {"center": v(599.34, 48.74) * mm, "radius": 1.59 * mm});
            skCircle(sketch, "E201.MirrorC", {"center": v(624.74, 17) * mm, "radius": 1.59 * mm});
            skCircle(sketch, "E202.MirrorC", {"center": v(643.79, 23.34) * mm, "radius": 1.59 * mm});
            skCircle(sketch, "E203.MirrorC", {"center": v(573.94, 55.1) * mm, "radius": 1.59 * mm});
            skCircle(sketch, "E204.MirrorC", {"center": v(586.64, 29.7) * mm, "radius": 1.59 * mm});
            skCircle(sketch, "E205.MirrorC", {"center": v(592.99, 80.5) * mm, "radius": 1.59 * mm});
            skCircle(sketch, "E206.MirrorC", {"center": v(650.14, 48.74) * mm, "radius": 1.59 * mm});
            skCircle(sketch, "E207.MirrorC", {"center": v(605.69, 86.84) * mm, "radius": 1.59 * mm});
            skCircle(sketch, "E208.MirrorC", {"center": v(592.99, 17) * mm, "radius": 1.59 * mm});
            skCircle(sketch, "E209.MirrorC", {"center": v(643.79, 42.4) * mm, "radius": 1.59 * mm});
            skCircle(sketch, "E210.MirrorC", {"center": v(567.59, 61.44) * mm, "radius": 1.59 * mm});
            skCircle(sketch, "E211.MirrorC", {"center": v(605.69, 17) * mm, "radius": 1.59 * mm});
            skCircle(sketch, "E212.MirrorC", {"center": v(656.49, 86.84) * mm, "radius": 1.59 * mm});
            skCircle(sketch, "E213.MirrorC", {"center": v(618.39, 61.44) * mm, "radius": 1.59 * mm});
            skCircle(sketch, "E214.MirrorC", {"center": v(605.69, 29.7) * mm, "radius": 1.59 * mm});
            skCircle(sketch, "E215.MirrorC", {"center": v(561.24, 99.54) * mm, "radius": 1.59 * mm});
            skCircle(sketch, "E216.MirrorC", {"center": v(618.39, 74.14) * mm, "radius": 1.59 * mm});
            skCircle(sketch, "E217.MirrorC", {"center": v(592.99, 36.04) * mm, "radius": 1.59 * mm});
            skCircle(sketch, "E218.MirrorC", {"center": v(656.49, 17) * mm, "radius": 1.59 * mm});
            skCircle(sketch, "E219.MirrorC", {"center": v(586.64, 99.54) * mm, "radius": 1.59 * mm});
            skCircle(sketch, "E220.MirrorC", {"center": v(599.34, 55.1) * mm, "radius": 1.59 * mm});
            skCircle(sketch, "E221.MirrorC", {"center": v(656.49, 61.44) * mm, "radius": 1.59 * mm});
            skCircle(sketch, "E222.MirrorC", {"center": v(637.44, 74.14) * mm, "radius": 1.59 * mm});
            skCircle(sketch, "E223.MirrorC", {"center": v(573.94, 105.9) * mm, "radius": 1.59 * mm});
            skCircle(sketch, "E224.MirrorC", {"center": v(624.74, 105.9) * mm, "radius": 1.59 * mm});
            skCircle(sketch, "E225.MirrorC", {"center": v(624.74, 29.7) * mm, "radius": 1.59 * mm});
            skCircle(sketch, "E226.MirrorC", {"center": v(586.64, 61.44) * mm, "radius": 1.59 * mm});
            skCircle(sketch, "E227.MirrorC", {"center": v(631.09, 10.64) * mm, "radius": 1.59 * mm});
            skCircle(sketch, "E228.MirrorC", {"center": v(586.64, 74.14) * mm, "radius": 1.59 * mm});
            skCircle(sketch, "E229.MirrorC", {"center": v(612.04, 23.34) * mm, "radius": 1.59 * mm});
            skCircle(sketch, "E230.MirrorC", {"center": v(656.49, 105.9) * mm, "radius": 1.59 * mm});
            skCircle(sketch, "E231.MirrorC", {"center": v(650.14, 67.8) * mm, "radius": 1.59 * mm});
            skCircle(sketch, "E232.MirrorC", {"center": v(605.69, 99.54) * mm, "radius": 1.59 * mm});
            skCircle(sketch, "E233.MirrorC", {"center": v(567.59, 99.54) * mm, "radius": 1.59 * mm});
            skCircle(sketch, "E234.MirrorC", {"center": v(662.84, 93.2) * mm, "radius": 1.59 * mm});
            skCircle(sketch, "E235.MirrorC", {"center": v(650.14, 86.84) * mm, "radius": 1.59 * mm});
            skCircle(sketch, "E236.MirrorC", {"center": v(605.69, 36.04) * mm, "radius": 1.59 * mm});
            skCircle(sketch, "E237.MirrorC", {"center": v(618.39, 17) * mm, "radius": 1.59 * mm});
            skCircle(sketch, "E238.MirrorC", {"center": v(580.29, 93.2) * mm, "radius": 1.59 * mm});
            skCircle(sketch, "E239.MirrorC", {"center": v(586.64, 36.04) * mm, "radius": 1.59 * mm});
            skCircle(sketch, "E240.MirrorC", {"center": v(561.24, 80.5) * mm, "radius": 1.59 * mm});
            skCircle(sketch, "E241.MirrorC", {"center": v(637.44, 42.4) * mm, "radius": 1.59 * mm});
            skCircle(sketch, "E242.MirrorC", {"center": v(631.09, 42.4) * mm, "radius": 1.59 * mm});
            skCircle(sketch, "E243.MirrorC", {"center": v(662.84, 61.44) * mm, "radius": 1.59 * mm});
            skCircle(sketch, "E244.MirrorC", {"center": v(573.94, 36.04) * mm, "radius": 1.59 * mm});
            skCircle(sketch, "E245.MirrorC", {"center": v(612.04, 17) * mm, "radius": 1.59 * mm});
            skCircle(sketch, "E246.MirrorC", {"center": v(567.59, 74.14) * mm, "radius": 1.59 * mm});
            skCircle(sketch, "E247.MirrorC", {"center": v(631.09, 55.1) * mm, "radius": 1.59 * mm});
            skCircle(sketch, "E248.MirrorC", {"center": v(631.09, 80.5) * mm, "radius": 1.59 * mm});
            skCircle(sketch, "E249.MirrorC", {"center": v(637.44, 48.74) * mm, "radius": 1.59 * mm});
            skCircle(sketch, "E250.MirrorC", {"center": v(662.84, 29.7) * mm, "radius": 1.59 * mm});
            skCircle(sketch, "E251.MirrorC", {"center": v(586.64, 67.8) * mm, "radius": 1.59 * mm});
            skCircle(sketch, "E252.MirrorC", {"center": v(650.14, 93.2) * mm, "radius": 1.59 * mm});
            skCircle(sketch, "E253.MirrorC", {"center": v(592.99, 48.74) * mm, "radius": 1.59 * mm});
            skCircle(sketch, "E254.MirrorC", {"center": v(586.64, 86.84) * mm, "radius": 1.59 * mm});
            skCircle(sketch, "E255.MirrorC", {"center": v(631.09, 74.14) * mm, "radius": 1.59 * mm});
            skCircle(sketch, "E256.MirrorC", {"center": v(580.29, 48.74) * mm, "radius": 1.59 * mm});
            skCircle(sketch, "E257.MirrorC", {"center": v(612.04, 55.1) * mm, "radius": 1.59 * mm});
            skCircle(sketch, "E258.MirrorC", {"center": v(612.04, 29.7) * mm, "radius": 1.59 * mm});
            skCircle(sketch, "E259.MirrorC", {"center": v(612.04, 105.9) * mm, "radius": 1.59 * mm});
            skCircle(sketch, "E260.MirrorC", {"center": v(573.94, 48.74) * mm, "radius": 1.59 * mm});
            skCircle(sketch, "E261.MirrorC", {"center": v(599.34, 74.14) * mm, "radius": 1.59 * mm});
            skCircle(sketch, "E262.MirrorC", {"center": v(605.69, 67.8) * mm, "radius": 1.59 * mm});
            skCircle(sketch, "E263.MirrorC", {"center": v(561.24, 61.44) * mm, "radius": 1.59 * mm});
            skCircle(sketch, "E264.MirrorC", {"center": v(643.79, 67.8) * mm, "radius": 1.59 * mm});
            skCircle(sketch, "E265.MirrorC", {"center": v(567.59, 80.5) * mm, "radius": 1.59 * mm});
            skCircle(sketch, "E266.MirrorC", {"center": v(624.74, 67.8) * mm, "radius": 1.59 * mm});
            skCircle(sketch, "E267.MirrorC", {"center": v(592.99, 86.84) * mm, "radius": 1.59 * mm});
            skCircle(sketch, "E268.MirrorC", {"center": v(631.09, 93.2) * mm, "radius": 1.59 * mm});
            skCircle(sketch, "E269.MirrorC", {"center": v(567.59, 4.3) * mm, "radius": 1.59 * mm});
            skCircle(sketch, "E270.MirrorC", {"center": v(637.44, 93.2) * mm, "radius": 1.59 * mm});
            skCircle(sketch, "E271.MirrorC", {"center": v(599.34, 99.54) * mm, "radius": 1.59 * mm});
            skCircle(sketch, "E272.MirrorC", {"center": v(580.29, 61.44) * mm, "radius": 1.59 * mm});
            skCircle(sketch, "E273.MirrorC", {"center": v(573.94, 23.34) * mm, "radius": 1.59 * mm});
            skCircle(sketch, "E274.MirrorC", {"center": v(624.74, 48.74) * mm, "radius": 1.59 * mm});
            skCircle(sketch, "E275.MirrorC", {"center": v(637.44, 55.1) * mm, "radius": 1.59 * mm});
            skCircle(sketch, "E276.MirrorC", {"center": v(599.34, 86.84) * mm, "radius": 1.59 * mm});
            skCircle(sketch, "E277.MirrorC", {"center": v(567.59, 93.2) * mm, "radius": 1.59 * mm});
            skCircle(sketch, "E278.MirrorC", {"center": v(643.79, 74.14) * mm, "radius": 1.59 * mm});
            skCircle(sketch, "E279.MirrorC", {"center": v(650.14, 10.64) * mm, "radius": 1.59 * mm});
            skCircle(sketch, "E280.MirrorC", {"center": v(650.14, 80.5) * mm, "radius": 1.59 * mm});
            skCircle(sketch, "E281.MirrorC", {"center": v(580.29, 99.54) * mm, "radius": 1.59 * mm});
            skCircle(sketch, "E282.MirrorC", {"center": v(637.44, 4.3) * mm, "radius": 1.59 * mm});
            skCircle(sketch, "E283.MirrorC", {"center": v(643.79, 10.64) * mm, "radius": 1.59 * mm});
            skCircle(sketch, "E284.MirrorC", {"center": v(643.79, 80.5) * mm, "radius": 1.59 * mm});
            skCircle(sketch, "E285.MirrorC", {"center": v(599.34, 61.44) * mm, "radius": 1.59 * mm});
            skCircle(sketch, "E286.MirrorC", {"center": v(637.44, 105.9) * mm, "radius": 1.59 * mm});
            skCircle(sketch, "E287.MirrorC", {"center": v(567.59, 86.84) * mm, "radius": 1.59 * mm});
            skCircle(sketch, "E288.MirrorC", {"center": v(561.24, 55.1) * mm, "radius": 1.59 * mm});
            skCircle(sketch, "E289.MirrorC", {"center": v(561.24, 36.04) * mm, "radius": 1.59 * mm});
            skCircle(sketch, "E290.MirrorC", {"center": v(650.14, 105.9) * mm, "radius": 1.59 * mm});
            skCircle(sketch, "E291.MirrorC", {"center": v(612.04, 4.3) * mm, "radius": 1.59 * mm});
            skCircle(sketch, "E292.MirrorC", {"center": v(612.04, 10.64) * mm, "radius": 1.59 * mm});
            skCircle(sketch, "E293.MirrorC", {"center": v(631.09, 99.54) * mm, "radius": 1.59 * mm});
            skCircle(sketch, "E294.MirrorC", {"center": v(624.74, 4.3) * mm, "radius": 1.59 * mm});
            skCircle(sketch, "E295.MirrorC", {"center": v(599.34, 105.9) * mm, "radius": 1.59 * mm});
            skCircle(sketch, "E296.MirrorC", {"center": v(624.74, 10.64) * mm, "radius": 1.59 * mm});
            skCircle(sketch, "E297.MirrorC", {"center": v(580.29, 4.3) * mm, "radius": 1.59 * mm});
            skCircle(sketch, "E298.MirrorC", {"center": v(580.29, 74.14) * mm, "radius": 1.59 * mm});
            skCircle(sketch, "E299.MirrorC", {"center": v(618.39, 29.7) * mm, "radius": 1.59 * mm});
            skCircle(sketch, "E300.MirrorC", {"center": v(656.49, 29.7) * mm, "radius": 1.59 * mm});
            skCircle(sketch, "E301.MirrorC", {"center": v(592.99, 42.4) * mm, "radius": 1.59 * mm});
            skCircle(sketch, "E302.MirrorC", {"center": v(599.34, 29.7) * mm, "radius": 1.59 * mm});
            skCircle(sketch, "E303.MirrorC", {"center": v(643.79, 29.7) * mm, "radius": 1.59 * mm});
            skCircle(sketch, "E304.MirrorC", {"center": v(567.59, 48.74) * mm, "radius": 1.59 * mm});
            skCircle(sketch, "E305.MirrorC", {"center": v(643.79, 99.54) * mm, "radius": 1.59 * mm});
            skCircle(sketch, "E306.MirrorC", {"center": v(618.39, 42.4) * mm, "radius": 1.59 * mm});
            skCircle(sketch, "E307.MirrorC", {"center": v(624.74, 80.5) * mm, "radius": 1.59 * mm});
            skCircle(sketch, "E308.MirrorC", {"center": v(662.84, 99.54) * mm, "radius": 1.59 * mm});
            skCircle(sketch, "E309.MirrorC", {"center": v(599.34, 36.04) * mm, "radius": 1.59 * mm});
            skCircle(sketch, "E310.MirrorC", {"center": v(599.34, 23.34) * mm, "radius": 1.59 * mm});
            skCircle(sketch, "E311.MirrorC", {"center": v(656.49, 55.1) * mm, "radius": 1.59 * mm});
            skCircle(sketch, "E312.MirrorC", {"center": v(637.44, 67.8) * mm, "radius": 1.59 * mm});
            skCircle(sketch, "E313.MirrorC", {"center": v(573.94, 61.44) * mm, "radius": 1.59 * mm});
            skCircle(sketch, "E314.MirrorC", {"center": v(612.04, 61.44) * mm, "radius": 1.59 * mm});
            skCircle(sketch, "E315.MirrorC", {"center": v(573.94, 4.3) * mm, "radius": 1.59 * mm});
            skCircle(sketch, "E316.MirrorC", {"center": v(624.74, 55.1) * mm, "radius": 1.59 * mm});
            skCircle(sketch, "E317.MirrorC", {"center": v(631.09, 4.3) * mm, "radius": 1.59 * mm});
            skCircle(sketch, "E318.MirrorC", {"center": v(650.14, 55.1) * mm, "radius": 1.59 * mm});
            skCircle(sketch, "E319.MirrorC", {"center": v(612.04, 42.4) * mm, "radius": 1.59 * mm});
            skCircle(sketch, "E320.MirrorC", {"center": v(605.69, 80.5) * mm, "radius": 1.59 * mm});
            skCircle(sketch, "E321.MirrorC", {"center": v(662.84, 55.1) * mm, "radius": 1.59 * mm});
            skCircle(sketch, "E322.MirrorC", {"center": v(624.74, 74.14) * mm, "radius": 1.59 * mm});
            skCircle(sketch, "E323.MirrorC", {"center": v(580.29, 55.1) * mm, "radius": 1.59 * mm});
            skCircle(sketch, "E324.MirrorC", {"center": v(656.49, 23.34) * mm, "radius": 1.59 * mm});
            skCircle(sketch, "E325.MirrorC", {"center": v(605.69, 93.2) * mm, "radius": 1.59 * mm});
            skCircle(sketch, "E326.MirrorC", {"center": v(656.49, 93.2) * mm, "radius": 1.59 * mm});
            skCircle(sketch, "E327.MirrorC", {"center": v(656.49, 74.14) * mm, "radius": 1.59 * mm});
            skCircle(sketch, "E328.MirrorC", {"center": v(612.04, 67.8) * mm, "radius": 1.59 * mm});
            skCircle(sketch, "E329.MirrorC", {"center": v(573.94, 80.5) * mm, "radius": 1.59 * mm});
            skCircle(sketch, "E330.MirrorC", {"center": v(580.29, 29.7) * mm, "radius": 1.59 * mm});
            skCircle(sketch, "E331.MirrorC", {"center": v(618.39, 80.5) * mm, "radius": 1.59 * mm});
            skCircle(sketch, "E332.MirrorC", {"center": v(592.99, 105.9) * mm, "radius": 1.59 * mm});
            skCircle(sketch, "E333.MirrorC", {"center": v(624.74, 99.54) * mm, "radius": 1.59 * mm});
            skCircle(sketch, "E334.MirrorC", {"center": v(656.49, 48.74) * mm, "radius": 1.59 * mm});
            skCircle(sketch, "E335.MirrorC", {"center": v(573.94, 10.64) * mm, "radius": 1.59 * mm});
            skCircle(sketch, "E336.MirrorC", {"center": v(586.64, 4.3) * mm, "radius": 1.59 * mm});
            skCircle(sketch, "E337.MirrorC", {"center": v(586.64, 23.34) * mm, "radius": 1.59 * mm});
            skCircle(sketch, "E338.MirrorC", {"center": v(561.24, 29.7) * mm, "radius": 1.59 * mm});
            skCircle(sketch, "E339.MirrorC", {"center": v(612.04, 93.2) * mm, "radius": 1.59 * mm});
            skCircle(sketch, "E340.MirrorC", {"center": v(662.84, 17) * mm, "radius": 1.59 * mm});
            skCircle(sketch, "E341.MirrorC", {"center": v(631.09, 86.84) * mm, "radius": 1.59 * mm});
            skCircle(sketch, "E342.MirrorC", {"center": v(592.99, 4.3) * mm, "radius": 1.59 * mm});
            skCircle(sketch, "E343.MirrorC", {"center": v(662.84, 67.8) * mm, "radius": 1.59 * mm});
            skCircle(sketch, "E344.MirrorC", {"center": v(567.59, 55.1) * mm, "radius": 1.59 * mm});
            skSolve(sketch);
        }
        {
            var Q0;
            Q0 = qSketchRegion(id + "F10", true);
            extrude(context, id + "F11", {"entities" : qUnion([Q0]), "operationType" : NewBodyOperationType.REMOVE, "endBound" : BoundingType.THROUGH_ALL, "oppositeDirection" : true, "depth" : 25.4 * mm, "offsetDistance" : 25.4 * mm});
        }
        {
            var Q0;
            Q0=qCreatedBy(makeId("Top.planeOp"),FACE);
            var sketch = newSketch(context, id + "F12", { "sketchPlane" : qUnion([Q0])});
            skLineSegment(sketch, "E345.bottom", {"start": v(-1279.3, 1834.21) * mm, "end": v(-60.1, 1834.21) * mm});
            skLineSegment(sketch, "E345.top", {"start": v(-1279.3, 1224.61) * mm, "end": v(-60.1, 1224.61) * mm});
            skLineSegment(sketch, "E345.left", {"start": v(-1279.3, 1834.21) * mm, "end": v(-1279.3, 1224.61) * mm});
            skLineSegment(sketch, "E345.right", {"start": v(-60.1, 1834.21) * mm, "end": v(-60.1, 1224.61) * mm});
            skSolve(sketch);
        }
        {
            var Q0;
            Q0=makeQuery(id+"F12.imprint","IMPRINT",FACE,{"disambiguationData":[TD([[makeQuery(id+"F12.imprint","IMPRINT",EDGE,{"derivedFrom":sQuery(id+"F12.wireOp",EDGE,"E345.bottom")}),-1.0]])]});
            var sketch = newSketch(context, id + "F13", { "sketchPlane" : qUnion([Q0])});
            skPoint(sketch, "E346", {"position": v(-364.9, 383.06) * mm});
            skLineSegment(sketch, "E347.bottom", {"start": v(-364.9, 383.06) * mm, "end": v(-104.55, 383.06) * mm});
            skLineSegment(sketch, "E347.top", {"start": v(-364.9, 671.63) * mm, "end": v(-104.55, 671.63) * mm});
            skLineSegment(sketch, "E347.left", {"start": v(-364.9, 383.06) * mm, "end": v(-364.9, 671.63) * mm});
            skLineSegment(sketch, "E347.right", {"start": v(-104.55, 383.06) * mm, "end": v(-104.55, 671.63) * mm});
            skLineSegment(sketch, "E348", {"start": v(-104.55, 527.34) * mm, "end": v(-364.9, 527.34) * mm, "construction": true});
            skLineSegment(sketch, "E349", {"start": v(-371.25, 560.8) * mm, "end": v(-371.25, 493.89) * mm});
            skPoint(sketch, "E350", {"position": v(-371.25, 527.34) * mm});
            skArc(sketch, "E351", {"start": v(-368.07, 566.3) * mm, "mid": v(-365.75, 568.62) * mm, "end": v(-364.9, 571.8) * mm});
            skArc(sketch, "E352.MirrorCS", {"start": v(-368.07, 488.39) * mm, "mid": v(-365.75, 486.07) * mm, "end": v(-364.9, 482.9) * mm});
            skPoint(sketch, "E353.visualSharp", {"position": v(-371.25, 565.44) * mm});
            skArc(sketch, "E353.filletArc", {"start": v(-368.07, 566.3) * mm, "mid": v(-370.4, 563.97) * mm, "end": v(-371.25, 560.8) * mm});
            skPoint(sketch, "E354.visualSharp", {"position": v(-371.25, 489.24) * mm});
            skArc(sketch, "E354.filletArc", {"start": v(-371.25, 493.89) * mm, "mid": v(-370.4, 490.71) * mm, "end": v(-368.07, 488.39) * mm});
            skSolve(sketch);
        }
        {
            var Q0;
            Q0 = qSketchRegion(id + "F13", true);
            extrude(context, id + "F14", {"entities" : qUnion([Q0]), "depth" : 3.17 * mm, "offsetDistance" : 25.4 * mm});
        }
        {
            var Q0;
            Q0=makeQuery(id+"F2.opExtrude","CAP_FACE",FACE,{"disambiguationData":[OSD([sQuery(id+"F1.wireOp",EDGE,"E5.bottom"),sQuery(id+"F1.wireOp",EDGE,"E5.top"),sQuery(id+"F1.wireOp",EDGE,"E5.left"),sQuery(id+"F1.wireOp",EDGE,"E5.right"),sQuery(id+"F1.wireOp",EDGE,"E9.bottom"),sQuery(id+"F1.wireOp",EDGE,"E9.top"),sQuery(id+"F1.wireOp",EDGE,"E9.right"),sQuery(id+"F1.wireOp",EDGE,"E10.trimOffspring")])],"isStart":false});
            var sketch = newSketch(context, id + "F15", { "sketchPlane" : qUnion([Q0])});
            skLineSegment(sketch, "E355", {"start": v(162.15, 71.9) * mm, "end": v(450.72, 71.9) * mm, "construction": true});
            skLineSegment(sketch, "E356", {"start": v(165.33, 71.9) * mm, "end": v(165.33, -112.24) * mm, "construction": true});
            skLineSegment(sketch, "E357", {"start": v(238.35, 71.9) * mm, "end": v(238.35, -112.24) * mm, "construction": true});
            skCircle(sketch, "E358", {"center": v(212.95, 55.88) * mm, "radius": 3.75 * mm});
            skCircle(sketch, "E359", {"center": v(181.2, 55.88) * mm, "radius": 12.7 * mm});
            skSolve(sketch);
        }
        {
            var Q0;
            Q0 = qSketchRegion(id + "F15", true);
            extrude(context, id + "F16", {"entities" : qUnion([Q0]), "operationType" : NewBodyOperationType.REMOVE, "endBound" : BoundingType.THROUGH_ALL, "oppositeDirection" : true, "depth" : 25.4 * mm, "offsetDistance" : 25.4 * mm});
        }
        {
            var Q0;
            Q0=makeQuery(id+"F5.opExtrude","SWEPT_EDGE",EDGE,{"disambiguationData":[OSD([sQuery(id+"F4.wireOp",EDGE,"E37.bottom"),sQuery(id+"F4.wireOp",EDGE,"E37.right")])]});
            var Q1;
            Q1=makeQuery(id+"F5.opExtrude","SWEPT_EDGE",EDGE,{"disambiguationData":[OSD([sQuery(id+"F4.wireOp",EDGE,"E37.bottom"),sQuery(id+"F4.wireOp",EDGE,"E37.left")])]});
            var Q2;
            Q2=makeQuery(id+"F5.opExtrude","SWEPT_EDGE",EDGE,{"disambiguationData":[OSD([sQuery(id+"F4.wireOp",EDGE,"E37.top"),sQuery(id+"F4.wireOp",EDGE,"E37.left")])]});
            var Q3;
            Q3=makeQuery(id+"F5.opExtrude","SWEPT_EDGE",EDGE,{"disambiguationData":[OSD([sQuery(id+"F4.wireOp",EDGE,"E37.top"),sQuery(id+"F4.wireOp",EDGE,"E37.right")])]});
            var Q4;
            Q4=makeQuery(id+"F5.opExtrude","SWEPT_EDGE",EDGE,{"disambiguationData":[OSD([sQuery(id+"F4.wireOp",EDGE,"E38.top"),sQuery(id+"F4.wireOp",EDGE,"E38.right")])]});
            var Q5;
            Q5=makeQuery(id+"F5.opExtrude","SWEPT_EDGE",EDGE,{"disambiguationData":[OSD([sQuery(id+"F4.wireOp",EDGE,"E38.top"),sQuery(id+"F4.wireOp",EDGE,"E38.left")])]});
            var Q6;
            Q6=makeQuery(id+"F5.opExtrude","SWEPT_EDGE",EDGE,{"disambiguationData":[OSD([sQuery(id+"F4.wireOp",EDGE,"E38.bottom"),sQuery(id+"F4.wireOp",EDGE,"E38.left")])]});
            var Q7;
            Q7=makeQuery(id+"F5.opExtrude","SWEPT_EDGE",EDGE,{"disambiguationData":[OSD([sQuery(id+"F4.wireOp",EDGE,"E38.bottom"),sQuery(id+"F4.wireOp",EDGE,"E38.right")])]});
            fillet(context, id + "F17", {"entities" : qUnion([Q0, Q1, Q2, Q3, Q4, Q5, Q6, Q7]), "radius" : 5.08 * mm, "tangentPropagation" : true, "allowEdgeOverflow" : false});
        }
        {
            var Q0;
            Q0 = qSketchRegion(id + "F10", true);
            extrude(context, id + "F18", {"entities" : qUnion([Q0]), "operationType" : NewBodyOperationType.REMOVE, "endBound" : BoundingType.THROUGH_ALL, "oppositeDirection" : true, "depth" : 25.4 * mm, "offsetDistance" : 25.4 * mm});
        }
    });
